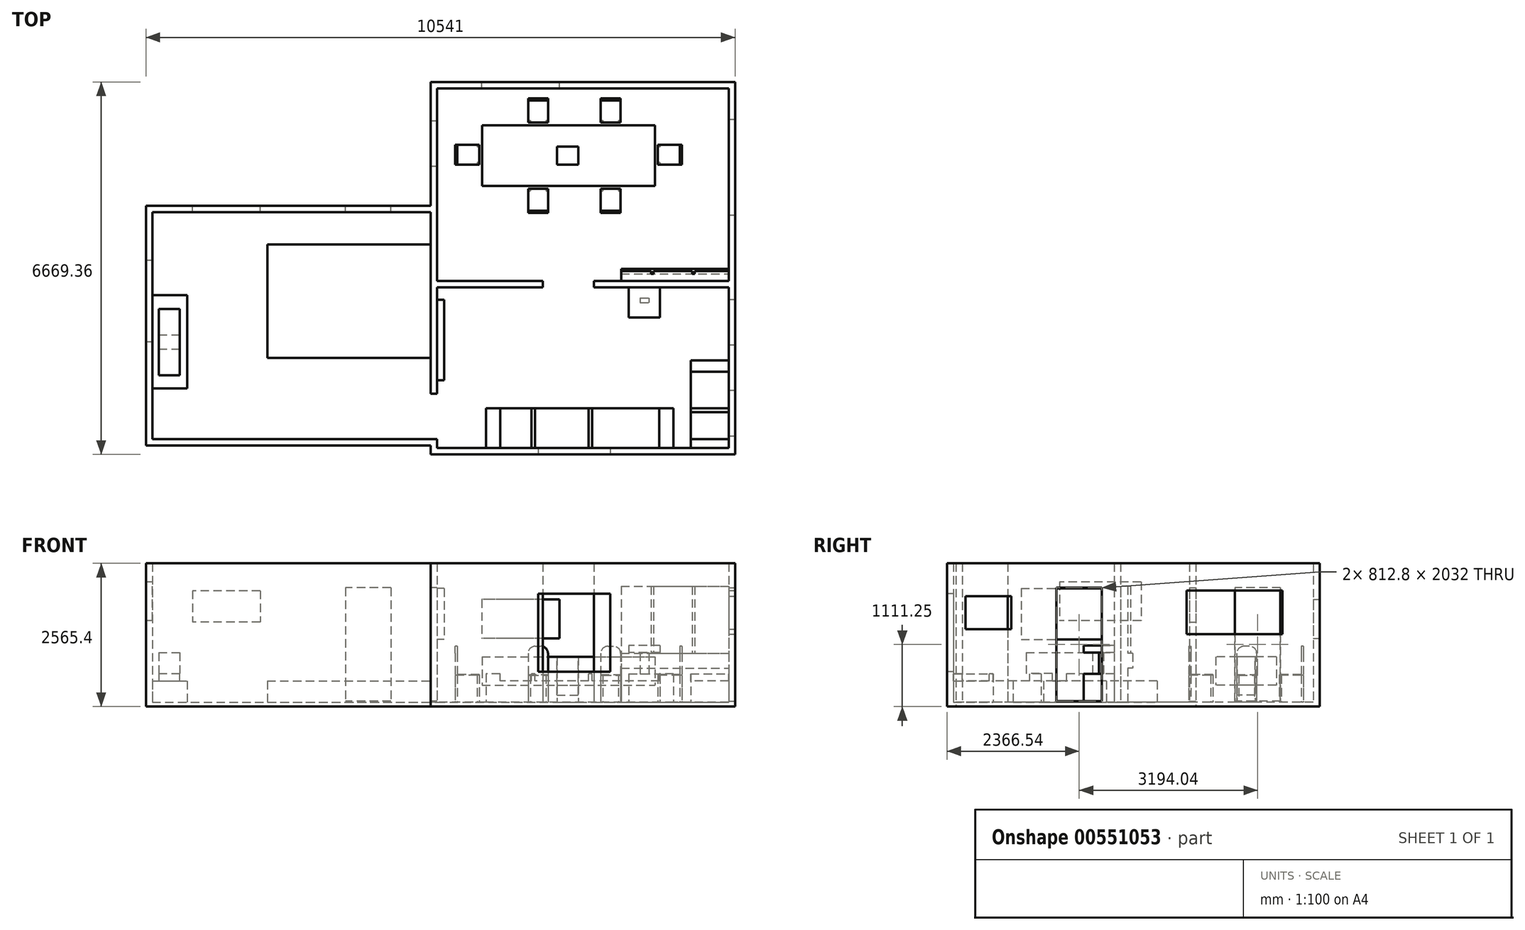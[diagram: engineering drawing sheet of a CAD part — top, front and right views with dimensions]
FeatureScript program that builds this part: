
annotation { "Feature Type Name" : "Feature", "Feature Type Description" : "" }
export const myFeature = defineFeature(function(context is Context, id is Id, definition is map)
    precondition{}
    {
        {
            var Q0;
            Q0=qCreatedBy(makeId("Top.planeOp"),FACE);
            var sketch = newSketch(context, id + "F0", { "sketchPlane" : qUnion([Q0])});
            skLineSegment(sketch, "E0", {"start": v(-1504.64, 2667.48) * mm, "end": v(-1504.64, -2915.57) * mm});
            skPoint(sketch, "E1.startSnap0", {"position": v(-1504.64, 0.48) * mm});
            skLineSegment(sketch, "E2", {"start": v(-1618.94, 335.63) * mm, "end": v(-1886.74, 335.63) * mm});
            skLineSegment(sketch, "E3", {"start": v(-6483.04, 335.63) * mm, "end": v(-6483.04, -3728.37) * mm});
            skLineSegment(sketch, "E4", {"start": v(-6483.04, -3728.37) * mm, "end": v(-1390.34, -3728.37) * mm});
            skLineSegment(sketch, "E5.0", {"start": v(-1618.94, 449.93) * mm, "end": v(-6597.34, 449.93) * mm});
            skLineSegment(sketch, "E6.0", {"start": v(-6597.34, 449.93) * mm, "end": v(-6597.34, -3842.67) * mm});
            skLineSegment(sketch, "E7.0", {"start": v(-6597.34, -3842.67) * mm, "end": v(-1504.64, -3842.67) * mm});
            skPoint(sketch, "E8.end.orphan", {"position": v(-1886.74, 335.63) * mm});
            skPoint(sketch, "E8.start.orphan", {"position": v(-2699.54, 335.63) * mm});
            skLineSegment(sketch, "E9.trimOffspring", {"start": v(-1886.74, 335.63) * mm, "end": v(-6483.04, 335.63) * mm});
            skLineSegment(sketch, "E10", {"start": v(-1618.94, 335.63) * mm, "end": v(-1504.64, 335.63) * mm});
            skLineSegment(sketch, "E11", {"start": v(-1390.34, 335.63) * mm, "end": v(-1390.34, -896.73) * mm});
            skLineSegment(sketch, "E12", {"start": v(-1390.34, 335.63) * mm, "end": v(-1390.34, 2553.18) * mm});
            skLineSegment(sketch, "E13", {"start": v(-1618.94, 449.93) * mm, "end": v(-1504.64, 449.93) * mm});
            skLineSegment(sketch, "E14", {"start": v(-1390.34, -3842.67) * mm, "end": v(-1390.34, -3728.37) * mm});
            skPoint(sketch, "E15.orphan", {"position": v(-1504.64, -3728.37) * mm});
            skLineSegment(sketch, "E16", {"start": v(-1390.34, -2915.57) * mm, "end": v(-1504.64, -2915.57) * mm});
            skLineSegment(sketch, "E17", {"start": v(-1390.34, 2667.48) * mm, "end": v(3943.66, 2667.48) * mm});
            skLineSegment(sketch, "E18", {"start": v(3943.66, 2667.48) * mm, "end": v(3943.66, -4001.88) * mm});
            skLineSegment(sketch, "E19", {"start": v(3943.66, -4001.88) * mm, "end": v(-1390.34, -4001.88) * mm});
            skLineSegment(sketch, "E20", {"start": v(-1390.34, -3887.58) * mm, "end": v(-1390.34, -3842.67) * mm});
            skLineSegment(sketch, "E21.0", {"start": v(-1390.34, -896.73) * mm, "end": v(505.29, -896.73) * mm});
            skLineSegment(sketch, "E22.0", {"start": v(-1390.34, -1011.03) * mm, "end": v(505.29, -1011.03) * mm});
            skLineSegment(sketch, "E23", {"start": v(1418.62, -1011.03) * mm, "end": v(1418.62, -896.73) * mm});
            skLineSegment(sketch, "E24.0", {"start": v(505.29, -1011.03) * mm, "end": v(505.29, -896.73) * mm});
            skLineSegment(sketch, "E25.0", {"start": v(3967.22, -3887.58) * mm, "end": v(3943.66, -3887.58) * mm});
            skLineSegment(sketch, "E26.0", {"start": v(3829.36, 2553.18) * mm, "end": v(3829.36, -896.73) * mm});
            skLineSegment(sketch, "E27.0", {"start": v(-1390.34, 2553.18) * mm, "end": v(3829.36, 2553.18) * mm});
            skLineSegment(sketch, "E28.trimOffspring", {"start": v(1418.62, -1011.03) * mm, "end": v(3829.36, -1011.03) * mm});
            skLineSegment(sketch, "E29.trimOffspring", {"start": v(1418.62, -896.73) * mm, "end": v(3829.36, -896.73) * mm});
            skLineSegment(sketch, "E30", {"start": v(-1504.64, 2667.48) * mm, "end": v(-1390.34, 2667.48) * mm});
            skLineSegment(sketch, "E31", {"start": v(-1390.34, -4001.88) * mm, "end": v(-1504.64, -4001.88) * mm});
            skLineSegment(sketch, "E32", {"start": v(-1504.64, -4001.88) * mm, "end": v(-1504.64, -3842.67) * mm});
            skLineSegment(sketch, "E33.trimOffspring", {"start": v(-1390.34, -1011.03) * mm, "end": v(-1390.34, -2915.57) * mm});
            skLineSegment(sketch, "E34.trimOffspring", {"start": v(3829.36, -3887.58) * mm, "end": v(-1390.34, -3887.58) * mm});
            skLineSegment(sketch, "E35.trimOffspring", {"start": v(3829.36, -1011.03) * mm, "end": v(3829.36, -3887.58) * mm});
            skSolve(sketch);
        }
        {
            var Q0;
            Q0=makeQuery(id+"F0.imprint","IMPRINT",FACE,{"disambiguationData":[TD([[makeQuery(id+"F0.imprint","IMPRINT",EDGE,{"derivedFrom":sQuery(id+"F0.wireOp",EDGE,"E2")}),-1.0]])]});
            extrude(context, id + "F1", {"entities" : qUnion([Q0]), "depth" : 2489.2 * mm, "offsetDistance" : 25.4 * mm});
        }
        {
            var Q0;
            {var subQ0=sQuery(id+"F0.wireOp",EDGE,"E0");Q0=makeQuery(id+"F1.opExtrude","SWEPT_FACE",FACE,{"disambiguationData":[OSD([subQ0]),TDD([makeQuery(id+"F0.imprint","IMPRINT",EDGE,{"disambiguationData":[TD([[makeQuery(id+"F0.imprint","INTERSECT",VERTEX,{"derivedFrom":[subQ0,sQuery(id+"F0.wireOp",EDGE,"E30")]}),-1.0]])],"derivedFrom":subQ0})])]});}
            var sketch = newSketch(context, id + "F2", { "sketchPlane" : qUnion([Q0])});
            skLineSegment(sketch, "E36.0.0", {"start": v(-2667.48, 0) * mm, "end": v(-449.93, 0) * mm});
            skLineSegment(sketch, "E36.0.1", {"start": v(-449.93, 0) * mm, "end": v(-449.93, 2489.2) * mm});
            skLineSegment(sketch, "E36.0.2", {"start": v(-449.93, 2489.2) * mm, "end": v(-2667.48, 2489.2) * mm});
            skLineSegment(sketch, "E36.0.3", {"start": v(-2667.48, 2489.2) * mm, "end": v(-2667.48, 0) * mm});
            skLineSegment(sketch, "E37.bottom", {"start": v(-1965.1, 19.05) * mm, "end": v(-1152.3, 19.05) * mm});
            skLineSegment(sketch, "E37.top", {"start": v(-1965.1, 2051.05) * mm, "end": v(-1152.3, 2051.05) * mm});
            skLineSegment(sketch, "E37.left", {"start": v(-1965.1, 19.05) * mm, "end": v(-1965.1, 2051.05) * mm});
            skLineSegment(sketch, "E37.right", {"start": v(-1152.3, 19.05) * mm, "end": v(-1152.3, 2051.05) * mm});
            skSolve(sketch);
        }
        {
            var Q0;
            Q0=makeQuery(id+"F2.imprint","IMPRINT",FACE,{"disambiguationData":[TD([[makeQuery(id+"F2.imprint","IMPRINT",EDGE,{"derivedFrom":sQuery(id+"F2.wireOp",EDGE,"E37.bottom")}),1.0]])]});
            extrude(context, id + "F3", {"entities" : qUnion([Q0]), "operationType" : NewBodyOperationType.REMOVE, "oppositeDirection" : true, "depth" : 1270 * mm, "offsetDistance" : 25.4 * mm});
        }
        {
            var Q0;
            Q0=makeQuery(id+"F1.opExtrude","SWEPT_FACE",FACE,{"disambiguationData":[OSD([sQuery(id+"F0.wireOp",EDGE,"E5.0"),sQuery(id+"F0.wireOp",EDGE,"E13")])]});
            var sketch = newSketch(context, id + "F4", { "sketchPlane" : qUnion([Q0])});
            skLineSegment(sketch, "E38.0", {"start": v(1504.64, 2489.2) * mm, "end": v(1504.64, 0) * mm});
            skLineSegment(sketch, "E39.0", {"start": v(6597.34, 2489.2) * mm, "end": v(1504.64, 2489.2) * mm});
            skLineSegment(sketch, "E40.0", {"start": v(6597.34, 0) * mm, "end": v(1504.64, 0) * mm});
            skLineSegment(sketch, "E41.bottom", {"start": v(2213.37, 2051.05) * mm, "end": v(3026.17, 2051.05) * mm});
            skLineSegment(sketch, "E41.top", {"start": v(2213.37, 19.05) * mm, "end": v(3026.17, 19.05) * mm});
            skLineSegment(sketch, "E41.left", {"start": v(2213.37, 2051.05) * mm, "end": v(2213.37, 19.05) * mm});
            skLineSegment(sketch, "E41.right", {"start": v(3026.17, 2051.05) * mm, "end": v(3026.17, 19.05) * mm});
            skLineSegment(sketch, "E42.bottom", {"start": v(4550.44, 1995.7) * mm, "end": v(5763.92, 1995.7) * mm});
            skLineSegment(sketch, "E42.top", {"start": v(4550.44, 1433.9) * mm, "end": v(5763.92, 1433.9) * mm});
            skLineSegment(sketch, "E42.left", {"start": v(4550.44, 1995.7) * mm, "end": v(4550.44, 1433.9) * mm});
            skLineSegment(sketch, "E42.right", {"start": v(5763.92, 1995.7) * mm, "end": v(5763.92, 1433.9) * mm});
            skSolve(sketch);
        }
        {
            var Q0;
            Q0=makeQuery(id+"F4.imprint","IMPRINT",FACE,{"disambiguationData":[TD([[makeQuery(id+"F4.imprint","IMPRINT",EDGE,{"derivedFrom":sQuery(id+"F4.wireOp",EDGE,"E41.bottom")}),-1.0]])]});
            var Q1;
            Q1=makeQuery(id+"F4.imprint","IMPRINT",FACE,{"disambiguationData":[TD([[makeQuery(id+"F4.imprint","IMPRINT",EDGE,{"derivedFrom":sQuery(id+"F4.wireOp",EDGE,"E42.bottom")}),-1.0]])]});
            extrude(context, id + "F5", {"entities" : qUnion([Q0, Q1]), "operationType" : NewBodyOperationType.REMOVE, "oppositeDirection" : true, "depth" : 508 * mm, "offsetDistance" : 25.4 * mm});
        }
        {
            var Q0;
            Q0=makeQuery(id+"F1.opExtrude","SWEPT_FACE",FACE,{"disambiguationData":[OSD([sQuery(id+"F0.wireOp",EDGE,"E17"),sQuery(id+"F0.wireOp",EDGE,"E30")])]});
            var sketch = newSketch(context, id + "F6", { "sketchPlane" : qUnion([Q0])});
            skLineSegment(sketch, "E43.0", {"start": v(1504.64, 2489.2) * mm, "end": v(-3943.66, 2489.2) * mm});
            skLineSegment(sketch, "E44.bottom", {"start": v(-805.35, 1839.46) * mm, "end": v(587.9, 1839.46) * mm});
            skLineSegment(sketch, "E44.top", {"start": v(-805.35, 1142.83) * mm, "end": v(587.9, 1142.83) * mm});
            skLineSegment(sketch, "E44.left", {"start": v(-805.35, 1839.46) * mm, "end": v(-805.35, 1142.83) * mm});
            skLineSegment(sketch, "E44.right", {"start": v(587.9, 1839.46) * mm, "end": v(587.9, 1142.83) * mm});
            skSolve(sketch);
        }
        {
            var Q0;
            Q0=makeQuery(id+"F6.imprint","IMPRINT",FACE,{"disambiguationData":[TD([[makeQuery(id+"F6.imprint","IMPRINT",EDGE,{"derivedFrom":sQuery(id+"F6.wireOp",EDGE,"E44.bottom")}),-1.0]])]});
            extrude(context, id + "F7", {"entities" : qUnion([Q0]), "operationType" : NewBodyOperationType.REMOVE, "oppositeDirection" : true, "depth" : 508 * mm, "offsetDistance" : 25.4 * mm});
        }
        {
            var Q0;
            Q0=makeQuery(id+"F1.opExtrude","SWEPT_FACE",FACE,{"disambiguationData":[OSD([sQuery(id+"F0.wireOp",EDGE,"E18")])]});
            var sketch = newSketch(context, id + "F8", { "sketchPlane" : qUnion([Q0])});
            skPoint(sketch, "E45.0", {"position": v(2553.18, 1244.6) * mm});
            skLineSegment(sketch, "E46.0", {"start": v(-896.73, 2489.2) * mm, "end": v(-896.73, 0) * mm});
            skLineSegment(sketch, "E47.0", {"start": v(2553.18, 2489.2) * mm, "end": v(2553.18, 0) * mm});
            skLineSegment(sketch, "E48.bottom", {"start": v(-2041.74, 2051.05) * mm, "end": v(-1228.94, 2051.05) * mm});
            skLineSegment(sketch, "E48.top", {"start": v(-2041.74, 19.05) * mm, "end": v(-1228.94, 19.05) * mm});
            skLineSegment(sketch, "E48.left", {"start": v(-2041.74, 2051.05) * mm, "end": v(-2041.74, 19.05) * mm});
            skLineSegment(sketch, "E48.right", {"start": v(-1228.94, 2051.05) * mm, "end": v(-1228.94, 19.05) * mm});
            skLineSegment(sketch, "E49.bottom", {"start": v(-248.45, 1994.32) * mm, "end": v(1166.3, 1994.32) * mm});
            skLineSegment(sketch, "E49.top", {"start": v(-248.45, 1469.1) * mm, "end": v(1166.3, 1469.1) * mm});
            skLineSegment(sketch, "E49.left", {"start": v(-248.45, 1994.32) * mm, "end": v(-248.45, 1469.1) * mm});
            skLineSegment(sketch, "E49.right", {"start": v(1166.3, 1994.32) * mm, "end": v(1166.3, 1469.1) * mm});
            skLineSegment(sketch, "E50.bottom", {"start": v(-3669.42, 1899.68) * mm, "end": v(-2850.85, 1899.68) * mm});
            skLineSegment(sketch, "E50.top", {"start": v(-3669.42, 1308.23) * mm, "end": v(-2850.85, 1308.23) * mm});
            skLineSegment(sketch, "E50.left", {"start": v(-3669.42, 1899.68) * mm, "end": v(-3669.42, 1308.23) * mm});
            skLineSegment(sketch, "E50.right", {"start": v(-2850.85, 1899.68) * mm, "end": v(-2850.85, 1308.23) * mm});
            skSolve(sketch);
        }
        {
            var Q0;
            Q0=makeQuery(id+"F1.opExtrude","SWEPT_FACE",FACE,{"disambiguationData":[OSD([sQuery(id+"F0.wireOp",EDGE,"E6.0")])]});
            var sketch = newSketch(context, id + "F9", { "sketchPlane" : qUnion([Q0])});
            skLineSegment(sketch, "E51.bottom", {"start": v(527.62, 2155.2) * mm, "end": v(1989.7, 2155.2) * mm});
            skLineSegment(sketch, "E51.top", {"start": v(527.62, 1464.37) * mm, "end": v(1989.7, 1464.37) * mm});
            skLineSegment(sketch, "E51.left", {"start": v(527.62, 2155.2) * mm, "end": v(527.62, 1464.37) * mm});
            skLineSegment(sketch, "E51.right", {"start": v(1989.7, 2155.2) * mm, "end": v(1989.7, 1464.37) * mm});
            skSolve(sketch);
        }
        {
            var Q0;
            Q0=makeQuery(id+"F9.imprint","IMPRINT",FACE,{"disambiguationData":[TD([[makeQuery(id+"F9.imprint","IMPRINT",EDGE,{"derivedFrom":sQuery(id+"F9.wireOp",EDGE,"E51.bottom")}),-1.0]])]});
            extrude(context, id + "F10", {"entities" : qUnion([Q0]), "operationType" : NewBodyOperationType.REMOVE, "oppositeDirection" : true, "depth" : 381 * mm, "offsetDistance" : 25.4 * mm});
        }
        {
            var Q0;
            Q0=makeQuery(id+"F1.opExtrude","CAP_FACE",FACE,{"disambiguationData":[OSD([sQuery(id+"F0.wireOp",EDGE,"E0"),sQuery(id+"F0.wireOp",EDGE,"E2"),sQuery(id+"F0.wireOp",EDGE,"E3"),sQuery(id+"F0.wireOp",EDGE,"E4"),sQuery(id+"F0.wireOp",EDGE,"E5.0"),sQuery(id+"F0.wireOp",EDGE,"E6.0"),sQuery(id+"F0.wireOp",EDGE,"E7.0"),sQuery(id+"F0.wireOp",EDGE,"E9.trimOffspring"),sQuery(id+"F0.wireOp",EDGE,"E10"),sQuery(id+"F0.wireOp",EDGE,"E11"),sQuery(id+"F0.wireOp",EDGE,"E12"),sQuery(id+"F0.wireOp",EDGE,"E13"),sQuery(id+"F0.wireOp",EDGE,"E14"),sQuery(id+"F0.wireOp",EDGE,"E16"),sQuery(id+"F0.wireOp",EDGE,"E17"),sQuery(id+"F0.wireOp",EDGE,"E18"),sQuery(id+"F0.wireOp",EDGE,"E19"),sQuery(id+"F0.wireOp",EDGE,"E20"),sQuery(id+"F0.wireOp",EDGE,"E21.0"),sQuery(id+"F0.wireOp",EDGE,"E22.0"),sQuery(id+"F0.wireOp",EDGE,"E23"),sQuery(id+"F0.wireOp",EDGE,"E24.0"),sQuery(id+"F0.wireOp",EDGE,"E26.0"),sQuery(id+"F0.wireOp",EDGE,"E27.0"),sQuery(id+"F0.wireOp",EDGE,"E28.trimOffspring"),sQuery(id+"F0.wireOp",EDGE,"E29.trimOffspring"),sQuery(id+"F0.wireOp",EDGE,"E30"),sQuery(id+"F0.wireOp",EDGE,"E31"),sQuery(id+"F0.wireOp",EDGE,"E32"),sQuery(id+"F0.wireOp",EDGE,"E33.trimOffspring"),sQuery(id+"F0.wireOp",EDGE,"E34.trimOffspring"),sQuery(id+"F0.wireOp",EDGE,"E35.trimOffspring")])],"isStart":true});
            var sketch = newSketch(context, id + "F11", { "sketchPlane" : qUnion([Q0])});
            skLineSegment(sketch, "E52.0", {"start": v(-6597.34, 3842.67) * mm, "end": v(-1504.64, 3842.67) * mm});
            skLineSegment(sketch, "E53.0", {"start": v(3943.66, 4001.88) * mm, "end": v(-1504.64, 4001.88) * mm});
            skLineSegment(sketch, "E54.0", {"start": v(-1504.64, 4001.88) * mm, "end": v(-1504.64, 3842.67) * mm});
            skLineSegment(sketch, "E55.0", {"start": v(-1504.64, -2667.48) * mm, "end": v(3943.66, -2667.48) * mm});
            skLineSegment(sketch, "E56.0", {"start": v(-1504.64, -2667.48) * mm, "end": v(-1504.64, -449.93) * mm});
            skLineSegment(sketch, "E57.0", {"start": v(-6597.34, -449.93) * mm, "end": v(-1504.64, -449.93) * mm});
            skLineSegment(sketch, "E58.0", {"start": v(-6597.34, -449.93) * mm, "end": v(-6597.34, 3842.67) * mm});
            skLineSegment(sketch, "E59.0", {"start": v(3943.66, -2667.48) * mm, "end": v(3943.66, 4001.88) * mm});
            skSolve(sketch);
        }
        {
            var Q0;
            Q0=makeQuery(id+"F8.imprint","IMPRINT",FACE,{"disambiguationData":[TD([[makeQuery(id+"F8.imprint","IMPRINT",EDGE,{"derivedFrom":sQuery(id+"F8.wireOp",EDGE,"E48.bottom")}),-1.0]])]});
            var Q1;
            Q1=makeQuery(id+"F8.imprint","IMPRINT",FACE,{"disambiguationData":[TD([[makeQuery(id+"F8.imprint","IMPRINT",EDGE,{"derivedFrom":sQuery(id+"F8.wireOp",EDGE,"E50.bottom")}),-1.0]])]});
            extrude(context, id + "F12", {"entities" : qUnion([Q0, Q1]), "operationType" : NewBodyOperationType.REMOVE, "oppositeDirection" : true, "depth" : 381 * mm, "offsetDistance" : 25.4 * mm});
        }
        {
            var Q0;
            Q0 = qSketchRegion(id + "F11", true);
            extrude(context, id + "F13", {"entities" : qUnion([Q0]), "operationType" : NewBodyOperationType.ADD, "depth" : 76.2 * mm, "offsetDistance" : 25.4 * mm});
        }
        {
            var Q0;
            Q0=makeQuery(id+"F13.opExtrude","CAP_FACE",FACE,{"disambiguationData":[OSD([sQuery(id+"F11.wireOp",EDGE,"E52.0"),sQuery(id+"F11.wireOp",EDGE,"E53.0"),sQuery(id+"F11.wireOp",EDGE,"E54.0"),sQuery(id+"F11.wireOp",EDGE,"E55.0"),sQuery(id+"F11.wireOp",EDGE,"E56.0"),sQuery(id+"F11.wireOp",EDGE,"E57.0"),sQuery(id+"F11.wireOp",EDGE,"E58.0"),sQuery(id+"F11.wireOp",EDGE,"E59.0")])],"isStart":true});
            var sketch = newSketch(context, id + "F14", { "sketchPlane" : qUnion([Q0])});
            skLineSegment(sketch, "E60.0", {"start": v(-6483.04, 335.63) * mm, "end": v(-1504.64, 335.63) * mm});
            skLineSegment(sketch, "E61.0.2", {"start": v(-1504.64, 335.63) * mm, "end": v(-6483.04, 335.63) * mm});
            skLineSegment(sketch, "E62.bottom", {"start": v(-6483.04, -2818.82) * mm, "end": v(-5860.4, -2818.82) * mm});
            skLineSegment(sketch, "E62.top", {"start": v(-6483.04, -1151.08) * mm, "end": v(-5860.4, -1151.08) * mm});
            skLineSegment(sketch, "E62.left", {"start": v(-6483.04, -2818.82) * mm, "end": v(-6483.04, -1151.08) * mm});
            skLineSegment(sketch, "E62.right", {"start": v(-5860.4, -2818.82) * mm, "end": v(-5860.4, -1151.08) * mm});
            skLineSegment(sketch, "E63.bottom", {"start": v(-4425.64, -2272.14) * mm, "end": v(-1504.64, -2272.14) * mm});
            skLineSegment(sketch, "E63.top", {"start": v(-4425.64, -240.14) * mm, "end": v(-1504.64, -240.14) * mm});
            skLineSegment(sketch, "E63.left", {"start": v(-4425.64, -2272.14) * mm, "end": v(-4425.64, -240.14) * mm});
            skLineSegment(sketch, "E63.right", {"start": v(-1504.64, -2272.14) * mm, "end": v(-1504.64, -240.14) * mm});
            skSolve(sketch);
        }
        {
            var Q0;
            Q0 = qSketchRegion(id + "F14", true);
            extrude(context, id + "F15", {"entities" : qUnion([Q0]), "operationType" : NewBodyOperationType.ADD, "depth" : 381 * mm, "offsetDistance" : 25.4 * mm});
        }
        {
            var Q0;
            Q0=makeQuery(id+"F15.opExtrude","CAP_FACE",FACE,{"disambiguationData":[OSD([sQuery(id+"F14.wireOp",EDGE,"E62.bottom"),sQuery(id+"F14.wireOp",EDGE,"E62.top"),sQuery(id+"F14.wireOp",EDGE,"E62.left"),sQuery(id+"F14.wireOp",EDGE,"E62.right")])],"isStart":false});
            var sketch = newSketch(context, id + "F16", { "sketchPlane" : qUnion([Q0])});
            skLineSegment(sketch, "E64.bottom", {"start": v(-6367.3, -2585.93) * mm, "end": v(-5994.87, -2585.93) * mm});
            skLineSegment(sketch, "E64.top", {"start": v(-6367.3, -1394.85) * mm, "end": v(-5994.87, -1394.85) * mm});
            skLineSegment(sketch, "E64.left", {"start": v(-6367.3, -2585.93) * mm, "end": v(-6367.3, -1394.85) * mm});
            skLineSegment(sketch, "E64.right", {"start": v(-5994.87, -2585.93) * mm, "end": v(-5994.87, -1394.85) * mm});
            skSolve(sketch);
        }
        {
            var Q0;
            Q0=makeQuery(id+"F16.imprint","IMPRINT",FACE,{"disambiguationData":[TD([[makeQuery(id+"F16.imprint","IMPRINT",EDGE,{"derivedFrom":sQuery(id+"F16.wireOp",EDGE,"E64.bottom")}),1.0]])]});
            extrude(context, id + "F17", {"entities" : qUnion([Q0]), "operationType" : NewBodyOperationType.ADD, "depth" : 508 * mm, "offsetDistance" : 25.4 * mm});
        }
        {
            var Q0;
            Q0=makeQuery(id+"F17.opExtrude","SWEPT_FACE",FACE,{"disambiguationData":[OSD([sQuery(id+"F16.wireOp",EDGE,"E64.right")])]});
            var sketch = newSketch(context, id + "F18", { "sketchPlane" : qUnion([Q0])});
            skLineSegment(sketch, "E65", {"start": v(-2117.39, 381) * mm, "end": v(-2117.39, 513.68) * mm});
            skLineSegment(sketch, "E66", {"start": v(-2117.39, 513.68) * mm, "end": v(-2585.93, 513.68) * mm});
            skLineSegment(sketch, "E67", {"start": v(-2585.93, 513.68) * mm, "end": v(-2585.93, 381) * mm});
            skLineSegment(sketch, "E68", {"start": v(-2585.93, 381) * mm, "end": v(-2117.39, 381) * mm});
            skLineSegment(sketch, "E69", {"start": v(-1863.39, 381) * mm, "end": v(-1863.39, 513.68) * mm});
            skLineSegment(sketch, "E70", {"start": v(-1863.39, 513.68) * mm, "end": v(-1394.85, 513.68) * mm});
            skLineSegment(sketch, "E71", {"start": v(-1394.85, 513.68) * mm, "end": v(-1394.85, 381) * mm});
            skLineSegment(sketch, "E72", {"start": v(-1394.85, 381) * mm, "end": v(-1863.39, 381) * mm});
            skSolve(sketch);
        }
        {
            var Q0;
            Q0=makeQuery(id+"F18.imprint","IMPRINT",FACE,{"disambiguationData":[TD([[makeQuery(id+"F18.imprint","IMPRINT",EDGE,{"derivedFrom":sQuery(id+"F18.wireOp",EDGE,"E65")}),1.0]])]});
            var Q1;
            Q1=makeQuery(id+"F18.imprint","IMPRINT",FACE,{"disambiguationData":[TD([[makeQuery(id+"F18.imprint","IMPRINT",EDGE,{"derivedFrom":sQuery(id+"F18.wireOp",EDGE,"E69")}),-1.0]])]});
            extrude(context, id + "F19", {"entities" : qUnion([Q0, Q1]), "operationType" : NewBodyOperationType.REMOVE, "oppositeDirection" : true, "depth" : 398.78 * mm, "offsetDistance" : 25.4 * mm});
        }
        {
            var Q0;
            Q0=makeQuery(id+"F13.boolean.opBoolean","MERGE",FACE,{"derivedFrom":[makeQuery(id+"F1.opExtrude","SWEPT_FACE",FACE,{"disambiguationData":[OSD([sQuery(id+"F0.wireOp",EDGE,"E18")])]}),makeQuery(id+"F13.opExtrude","SWEPT_FACE",FACE,{"disambiguationData":[OSD([sQuery(id+"F11.wireOp",EDGE,"E59.0")])]})]});
            var sketch = newSketch(context, id + "F20", { "sketchPlane" : qUnion([Q0])});
            skLineSegment(sketch, "E73.bottom", {"start": v(285.24, 1999.45) * mm, "end": v(1998.27, 1999.45) * mm});
            skLineSegment(sketch, "E73.top", {"start": v(285.24, 1223.23) * mm, "end": v(1998.27, 1223.23) * mm});
            skLineSegment(sketch, "E73.left", {"start": v(285.24, 1999.45) * mm, "end": v(285.24, 1223.23) * mm});
            skLineSegment(sketch, "E73.right", {"start": v(1998.27, 1999.45) * mm, "end": v(1998.27, 1223.23) * mm});
            skSolve(sketch);
        }
        {
            var Q0;
            Q0=makeQuery(id+"F20.imprint","IMPRINT",FACE,{"disambiguationData":[TD([[makeQuery(id+"F20.imprint","IMPRINT",EDGE,{"derivedFrom":sQuery(id+"F20.wireOp",EDGE,"E73.bottom")}),-1.0]])]});
            extrude(context, id + "F21", {"entities" : qUnion([Q0]), "operationType" : NewBodyOperationType.REMOVE, "oppositeDirection" : true, "depth" : 508 * mm, "offsetDistance" : 25.4 * mm});
        }
        {
            var Q0;
            Q0=makeQuery(id+"F13.boolean.opBoolean","MERGE",FACE,{"derivedFrom":[makeQuery(id+"F1.opExtrude","SWEPT_FACE",FACE,{"disambiguationData":[OSD([sQuery(id+"F0.wireOp",EDGE,"E19"),sQuery(id+"F0.wireOp",EDGE,"E31")])]}),makeQuery(id+"F13.opExtrude","SWEPT_FACE",FACE,{"disambiguationData":[OSD([sQuery(id+"F11.wireOp",EDGE,"E53.0")])]})]});
            var sketch = newSketch(context, id + "F22", { "sketchPlane" : qUnion([Q0])});
            skLineSegment(sketch, "E74.bottom", {"start": v(418.78, 1942.4) * mm, "end": v(1713.72, 1942.4) * mm});
            skLineSegment(sketch, "E74.top", {"start": v(418.78, 545.4) * mm, "end": v(1713.72, 545.4) * mm});
            skLineSegment(sketch, "E74.left", {"start": v(418.78, 1942.4) * mm, "end": v(418.78, 545.4) * mm});
            skLineSegment(sketch, "E74.right", {"start": v(1713.72, 1942.4) * mm, "end": v(1713.72, 545.4) * mm});
            skSolve(sketch);
        }
        {
            var Q0;
            Q0=makeQuery(id+"F22.imprint","IMPRINT",FACE,{"disambiguationData":[TD([[makeQuery(id+"F22.imprint","IMPRINT",EDGE,{"derivedFrom":sQuery(id+"F22.wireOp",EDGE,"E74.bottom")}),-1.0]])]});
            extrude(context, id + "F23", {"entities" : qUnion([Q0]), "operationType" : NewBodyOperationType.REMOVE, "oppositeDirection" : true, "depth" : 254 * mm, "offsetDistance" : 25.4 * mm});
        }
        {
            var Q0;
            Q0=makeQuery(id+"F1.opExtrude","SWEPT_FACE",FACE,{"disambiguationData":[OSD([sQuery(id+"F0.wireOp",EDGE,"E33.trimOffspring")])]});
            var sketch = newSketch(context, id + "F24", { "sketchPlane" : qUnion([Q0])});
            skLineSegment(sketch, "E75.bottom", {"start": v(-2675, 2039.3) * mm, "end": v(-1233.72, 2039.3) * mm});
            skLineSegment(sketch, "E75.top", {"start": v(-2675, 1123.92) * mm, "end": v(-1233.72, 1123.92) * mm});
            skLineSegment(sketch, "E75.left", {"start": v(-2675, 2039.3) * mm, "end": v(-2675, 1123.92) * mm});
            skLineSegment(sketch, "E75.right", {"start": v(-1233.72, 2039.3) * mm, "end": v(-1233.72, 1123.92) * mm});
            skSolve(sketch);
        }
        {
            var Q0;
            Q0=makeQuery(id+"F24.imprint","IMPRINT",FACE,{"disambiguationData":[TD([[makeQuery(id+"F24.imprint","IMPRINT",EDGE,{"derivedFrom":sQuery(id+"F24.wireOp",EDGE,"E75.bottom")}),-1.0]])]});
            extrude(context, id + "F25", {"entities" : qUnion([Q0]), "operationType" : NewBodyOperationType.ADD, "depth" : 127 * mm, "offsetDistance" : 25.4 * mm});
        }
        {
            var Q0;
            Q0=makeQuery(id+"F13.opExtrude","CAP_FACE",FACE,{"disambiguationData":[OSD([sQuery(id+"F11.wireOp",EDGE,"E52.0"),sQuery(id+"F11.wireOp",EDGE,"E53.0"),sQuery(id+"F11.wireOp",EDGE,"E54.0"),sQuery(id+"F11.wireOp",EDGE,"E55.0"),sQuery(id+"F11.wireOp",EDGE,"E56.0"),sQuery(id+"F11.wireOp",EDGE,"E57.0"),sQuery(id+"F11.wireOp",EDGE,"E58.0"),sQuery(id+"F11.wireOp",EDGE,"E59.0")])],"isStart":true});
            var sketch = newSketch(context, id + "F26", { "sketchPlane" : qUnion([Q0])});
            skLineSegment(sketch, "E76.bottom", {"start": v(2842.39, -3887.58) * mm, "end": v(-513.06, -3887.58) * mm});
            skLineSegment(sketch, "E76.top", {"start": v(2842.39, -3173.13) * mm, "end": v(-513.06, -3173.13) * mm});
            skLineSegment(sketch, "E76.left", {"start": v(2842.39, -3887.58) * mm, "end": v(2842.39, -3173.13) * mm});
            skLineSegment(sketch, "E76.right", {"start": v(-513.06, -3887.58) * mm, "end": v(-513.06, -3173.13) * mm});
            skSolve(sketch);
        }
        {
            var Q0;
            Q0=makeQuery(id+"F26.imprint","IMPRINT",FACE,{"disambiguationData":[TD([[makeQuery(id+"F26.imprint","IMPRINT",EDGE,{"derivedFrom":sQuery(id+"F26.wireOp",EDGE,"E76.bottom")}),-1.0]])]});
            extrude(context, id + "F27", {"entities" : qUnion([Q0]), "operationType" : NewBodyOperationType.ADD, "depth" : 508 * mm, "offsetDistance" : 25.4 * mm});
        }
        {
            var Q0;
            Q0=makeQuery(id+"F27.opExtrude","CAP_FACE",FACE,{"disambiguationData":[OSD([sQuery(id+"F26.wireOp",EDGE,"E76.bottom"),sQuery(id+"F26.wireOp",EDGE,"E76.top"),sQuery(id+"F26.wireOp",EDGE,"E76.left"),sQuery(id+"F26.wireOp",EDGE,"E76.right")])],"isStart":false});
            var sketch = newSketch(context, id + "F28", { "sketchPlane" : qUnion([Q0])});
            skLineSegment(sketch, "E77.bottom", {"start": v(2588.39, -3887.58) * mm, "end": v(1387.88, -3887.58) * mm});
            skLineSegment(sketch, "E77.top", {"start": v(2588.39, -3173.13) * mm, "end": v(1387.88, -3173.13) * mm});
            skLineSegment(sketch, "E77.left", {"start": v(2588.39, -3887.58) * mm, "end": v(2588.39, -3173.13) * mm});
            skLineSegment(sketch, "E77.right", {"start": v(1387.88, -3887.58) * mm, "end": v(1387.88, -3173.13) * mm});
            skLineSegment(sketch, "E78.bottom", {"start": v(1324.38, -3887.58) * mm, "end": v(362.76, -3887.58) * mm});
            skLineSegment(sketch, "E78.top", {"start": v(1324.38, -3173.13) * mm, "end": v(362.76, -3173.13) * mm});
            skLineSegment(sketch, "E78.left", {"start": v(1324.38, -3887.58) * mm, "end": v(1324.38, -3173.13) * mm});
            skLineSegment(sketch, "E78.right", {"start": v(362.76, -3887.58) * mm, "end": v(362.76, -3173.13) * mm});
            skLineSegment(sketch, "E79.bottom", {"start": v(299.26, -3887.58) * mm, "end": v(-259.06, -3887.58) * mm});
            skLineSegment(sketch, "E79.top", {"start": v(299.26, -3173.13) * mm, "end": v(-259.06, -3173.13) * mm});
            skLineSegment(sketch, "E79.left", {"start": v(299.26, -3887.58) * mm, "end": v(299.26, -3173.13) * mm});
            skLineSegment(sketch, "E79.right", {"start": v(-259.06, -3887.58) * mm, "end": v(-259.06, -3173.13) * mm});
            skSolve(sketch);
        }
        {
            var Q0;
            Q0 = qSketchRegion(id + "F28", true);
            extrude(context, id + "F29", {"entities" : qUnion([Q0]), "operationType" : NewBodyOperationType.REMOVE, "oppositeDirection" : true, "depth" : 127 * mm, "offsetDistance" : 25.4 * mm});
        }
        {
            var Q0;
            Q0=makeQuery(id+"F13.opExtrude","CAP_FACE",FACE,{"disambiguationData":[OSD([sQuery(id+"F11.wireOp",EDGE,"E52.0"),sQuery(id+"F11.wireOp",EDGE,"E53.0"),sQuery(id+"F11.wireOp",EDGE,"E54.0"),sQuery(id+"F11.wireOp",EDGE,"E55.0"),sQuery(id+"F11.wireOp",EDGE,"E56.0"),sQuery(id+"F11.wireOp",EDGE,"E57.0"),sQuery(id+"F11.wireOp",EDGE,"E58.0"),sQuery(id+"F11.wireOp",EDGE,"E59.0")])],"isStart":true});
            var sketch = newSketch(context, id + "F30", { "sketchPlane" : qUnion([Q0])});
            skLineSegment(sketch, "E80.bottom", {"start": v(3829.36, -2317.58) * mm, "end": v(3150.51, -2317.58) * mm});
            skLineSegment(sketch, "E80.top", {"start": v(3829.36, -3887.58) * mm, "end": v(3150.51, -3887.58) * mm});
            skLineSegment(sketch, "E80.left", {"start": v(3829.36, -2317.58) * mm, "end": v(3829.36, -3887.58) * mm});
            skLineSegment(sketch, "E80.right", {"start": v(3150.51, -2317.58) * mm, "end": v(3150.51, -3887.58) * mm});
            skSolve(sketch);
        }
        {
            var Q0;
            Q0 = qSketchRegion(id + "F30", true);
            extrude(context, id + "F31", {"entities" : qUnion([Q0]), "operationType" : NewBodyOperationType.ADD, "depth" : 508 * mm, "offsetDistance" : 25.4 * mm});
        }
        {
            var Q0;
            Q0=makeQuery(id+"F31.opExtrude","CAP_FACE",FACE,{"disambiguationData":[OSD([sQuery(id+"F30.wireOp",EDGE,"E80.bottom"),sQuery(id+"F30.wireOp",EDGE,"E80.top"),sQuery(id+"F30.wireOp",EDGE,"E80.left"),sQuery(id+"F30.wireOp",EDGE,"E80.right")])],"isStart":false});
            var sketch = newSketch(context, id + "F32", { "sketchPlane" : qUnion([Q0])});
            skLineSegment(sketch, "E81.bottom", {"start": v(3150.51, -2521.52) * mm, "end": v(3829.36, -2521.52) * mm});
            skLineSegment(sketch, "E81.top", {"start": v(3150.51, -3175.93) * mm, "end": v(3829.36, -3175.93) * mm});
            skLineSegment(sketch, "E81.left", {"start": v(3150.51, -2521.52) * mm, "end": v(3150.51, -3175.93) * mm});
            skLineSegment(sketch, "E81.right", {"start": v(3829.36, -2521.52) * mm, "end": v(3829.36, -3175.93) * mm});
            skLineSegment(sketch, "E82.bottom", {"start": v(3829.36, -3245.4) * mm, "end": v(3150.51, -3245.4) * mm});
            skLineSegment(sketch, "E82.top", {"start": v(3829.36, -3729.8) * mm, "end": v(3150.51, -3729.8) * mm});
            skLineSegment(sketch, "E82.left", {"start": v(3829.36, -3245.4) * mm, "end": v(3829.36, -3729.8) * mm});
            skLineSegment(sketch, "E82.right", {"start": v(3150.51, -3245.4) * mm, "end": v(3150.51, -3729.8) * mm});
            skSolve(sketch);
        }
        {
            var Q0;
            Q0 = qSketchRegion(id + "F32", true);
            extrude(context, id + "F33", {"entities" : qUnion([Q0]), "operationType" : NewBodyOperationType.REMOVE, "oppositeDirection" : true, "depth" : 127 * mm, "offsetDistance" : 25.4 * mm});
        }
        {
            var Q0;
            Q0=makeQuery(id+"F13.opExtrude","CAP_FACE",FACE,{"disambiguationData":[OSD([sQuery(id+"F11.wireOp",EDGE,"E52.0"),sQuery(id+"F11.wireOp",EDGE,"E53.0"),sQuery(id+"F11.wireOp",EDGE,"E54.0"),sQuery(id+"F11.wireOp",EDGE,"E55.0"),sQuery(id+"F11.wireOp",EDGE,"E56.0"),sQuery(id+"F11.wireOp",EDGE,"E57.0"),sQuery(id+"F11.wireOp",EDGE,"E58.0"),sQuery(id+"F11.wireOp",EDGE,"E59.0")])],"isStart":true});
            var sketch = newSketch(context, id + "F34", { "sketchPlane" : qUnion([Q0])});
            skLineSegment(sketch, "E83.bottom", {"start": v(2040.86, -1011.03) * mm, "end": v(2599.87, -1011.03) * mm});
            skLineSegment(sketch, "E83.top", {"start": v(2040.86, -1553.24) * mm, "end": v(2599.87, -1553.24) * mm});
            skLineSegment(sketch, "E83.left", {"start": v(2040.86, -1011.03) * mm, "end": v(2040.86, -1553.24) * mm});
            skLineSegment(sketch, "E83.right", {"start": v(2599.87, -1011.03) * mm, "end": v(2599.87, -1553.24) * mm});
            skSolve(sketch);
        }
        {
            var Q0;
            Q0 = qSketchRegion(id + "F34", true);
            extrude(context, id + "F35", {"entities" : qUnion([Q0]), "operationType" : NewBodyOperationType.ADD, "depth" : 508 * mm, "offsetDistance" : 25.4 * mm});
        }
        {
            var Q0;
            Q0=makeQuery(id+"F35.opExtrude","CAP_FACE",FACE,{"disambiguationData":[OSD([sQuery(id+"F34.wireOp",EDGE,"E83.bottom"),sQuery(id+"F34.wireOp",EDGE,"E83.top"),sQuery(id+"F34.wireOp",EDGE,"E83.left"),sQuery(id+"F34.wireOp",EDGE,"E83.right")])],"isStart":false});
            var sketch = newSketch(context, id + "F36", { "sketchPlane" : qUnion([Q0])});
            skPoint(sketch, "E84.oppositeSnap0", {"position": v(2040.86, -1282.14) * mm});
            skLineSegment(sketch, "E84.bottom", {"start": v(2243.9, -1202.24) * mm, "end": v(2404.3, -1202.24) * mm});
            skLineSegment(sketch, "E84.top", {"start": v(2243.9, -1282.14) * mm, "end": v(2404.3, -1282.14) * mm});
            skLineSegment(sketch, "E84.left", {"start": v(2243.9, -1202.24) * mm, "end": v(2243.9, -1282.14) * mm});
            skLineSegment(sketch, "E84.right", {"start": v(2404.3, -1202.24) * mm, "end": v(2404.3, -1282.14) * mm});
            skSolve(sketch);
        }
        {
            var Q0;
            Q0 = qSketchRegion(id + "F36", true);
            extrude(context, id + "F37", {"entities" : qUnion([Q0]), "operationType" : NewBodyOperationType.ADD, "depth" : 381 * mm, "offsetDistance" : 25.4 * mm});
        }
        {
            var Q0;
            Q0=makeQuery(id+"F37.opExtrude","CAP_FACE",FACE,{"disambiguationData":[OSD([sQuery(id+"F36.wireOp",EDGE,"E84.bottom"),sQuery(id+"F36.wireOp",EDGE,"E84.top"),sQuery(id+"F36.wireOp",EDGE,"E84.left"),sQuery(id+"F36.wireOp",EDGE,"E84.right")])],"isStart":false});
            var sketch = newSketch(context, id + "F38", { "sketchPlane" : qUnion([Q0])});
            skLineSegment(sketch, "E85.0.0", {"start": v(2599.87, -1553.24) * mm, "end": v(2599.87, -1011.03) * mm});
            skLineSegment(sketch, "E85.0.1", {"start": v(2599.87, -1011.03) * mm, "end": v(2040.86, -1011.03) * mm});
            skLineSegment(sketch, "E85.0.2", {"start": v(2040.86, -1011.03) * mm, "end": v(2040.86, -1553.24) * mm});
            skLineSegment(sketch, "E85.0.3", {"start": v(2040.86, -1553.24) * mm, "end": v(2599.87, -1553.24) * mm});
            skLineSegment(sketch, "E86.bottom", {"start": v(2040.86, -1011.03) * mm, "end": v(2599.87, -1011.03) * mm});
            skLineSegment(sketch, "E86.right", {"start": v(2599.87, -1011.03) * mm, "end": v(2599.87, -1553.24) * mm});
            skSolve(sketch);
        }
        {
            var Q0;
            Q0 = qSketchRegion(id + "F38", true);
            extrude(context, id + "F39", {"entities" : qUnion([Q0]), "operationType" : NewBodyOperationType.ADD, "depth" : 127 * mm, "offsetDistance" : 25.4 * mm});
        }
        {
            var Q0;
            Q0=makeQuery(id+"F13.opExtrude","CAP_FACE",FACE,{"disambiguationData":[OSD([sQuery(id+"F11.wireOp",EDGE,"E52.0"),sQuery(id+"F11.wireOp",EDGE,"E53.0"),sQuery(id+"F11.wireOp",EDGE,"E54.0"),sQuery(id+"F11.wireOp",EDGE,"E55.0"),sQuery(id+"F11.wireOp",EDGE,"E56.0"),sQuery(id+"F11.wireOp",EDGE,"E57.0"),sQuery(id+"F11.wireOp",EDGE,"E58.0"),sQuery(id+"F11.wireOp",EDGE,"E59.0")])],"isStart":true});
            var sketch = newSketch(context, id + "F40", { "sketchPlane" : qUnion([Q0])});
            skLineSegment(sketch, "E87.bottom", {"start": v(755.04, 1511.24) * mm, "end": v(1140.64, 1511.24) * mm});
            skLineSegment(sketch, "E87.top", {"start": v(755.04, 1187.97) * mm, "end": v(1140.64, 1187.97) * mm});
            skLineSegment(sketch, "E87.left", {"start": v(755.04, 1511.24) * mm, "end": v(755.04, 1187.97) * mm});
            skLineSegment(sketch, "E87.right", {"start": v(1140.64, 1511.24) * mm, "end": v(1140.64, 1187.97) * mm});
            skSolve(sketch);
        }
        {
            var Q0;
            Q0 = qSketchRegion(id + "F40", true);
            extrude(context, id + "F41", {"entities" : qUnion([Q0]), "operationType" : NewBodyOperationType.ADD, "depth" : 304.8 * mm, "offsetDistance" : 25.4 * mm});
        }
        {
            var Q0;
            Q0=makeQuery(id+"F41.opExtrude","CAP_FACE",FACE,{"disambiguationData":[OSD([sQuery(id+"F40.wireOp",EDGE,"E87.bottom"),sQuery(id+"F40.wireOp",EDGE,"E87.top"),sQuery(id+"F40.wireOp",EDGE,"E87.left"),sQuery(id+"F40.wireOp",EDGE,"E87.right")])],"isStart":false});
            var sketch = newSketch(context, id + "F42", { "sketchPlane" : qUnion([Q0])});
            skLineSegment(sketch, "E88.0.0", {"start": v(755.04, 1511.24) * mm, "end": v(755.04, 1187.97) * mm});
            skLineSegment(sketch, "E88.0.1", {"start": v(755.04, 1187.97) * mm, "end": v(1140.64, 1187.97) * mm});
            skLineSegment(sketch, "E88.0.2", {"start": v(1140.64, 1187.97) * mm, "end": v(1140.64, 1511.24) * mm});
            skLineSegment(sketch, "E88.0.3", {"start": v(1140.64, 1511.24) * mm, "end": v(755.04, 1511.24) * mm});
            skLineSegment(sketch, "E89.bottom", {"start": v(-583.52, 1892.24) * mm, "end": v(2513.74, 1892.24) * mm});
            skLineSegment(sketch, "E89.top", {"start": v(-583.52, 806.97) * mm, "end": v(2513.74, 806.97) * mm});
            skLineSegment(sketch, "E89.left", {"start": v(-583.52, 1892.24) * mm, "end": v(-583.52, 806.97) * mm});
            skLineSegment(sketch, "E89.right", {"start": v(2513.74, 1892.24) * mm, "end": v(2513.74, 806.97) * mm});
            skSolve(sketch);
        }
        {
            var Q0;
            Q0=makeQuery(id+"F42.imprint","IMPRINT",FACE,{"disambiguationData":[TD([[makeQuery(id+"F42.imprint","IMPRINT",EDGE,{"derivedFrom":sQuery(id+"F42.wireOp",EDGE,"E88.0.0")}),-1.0]])]});
            extrude(context, id + "F43", {"entities" : qUnion([Q0]), "depth" : 508 * mm, "offsetDistance" : 25.4 * mm});
        }
        {
            var Q0;
            Q0=makeQuery(id+"F43.opExtrude","CAP_FACE",FACE,{"disambiguationData":[OSD([sQuery(id+"F42.wireOp",EDGE,"E88.0.0"),sQuery(id+"F42.wireOp",EDGE,"E88.0.1"),sQuery(id+"F42.wireOp",EDGE,"E88.0.2"),sQuery(id+"F42.wireOp",EDGE,"E88.0.3"),sQuery(id+"F42.wireOp",EDGE,"E89.bottom"),sQuery(id+"F42.wireOp",EDGE,"E89.top"),sQuery(id+"F42.wireOp",EDGE,"E89.left"),sQuery(id+"F42.wireOp",EDGE,"E89.right")])],"isStart":false});
            var sketch = newSketch(context, id + "F44", { "sketchPlane" : qUnion([Q0])});
            skLineSegment(sketch, "E90.bottom", {"start": v(755.04, 1511.24) * mm, "end": v(1140.64, 1511.24) * mm});
            skLineSegment(sketch, "E90.top", {"start": v(755.04, 1187.97) * mm, "end": v(1140.64, 1187.97) * mm});
            skLineSegment(sketch, "E90.left", {"start": v(755.04, 1511.24) * mm, "end": v(755.04, 1187.97) * mm});
            skLineSegment(sketch, "E90.right", {"start": v(1140.64, 1511.24) * mm, "end": v(1140.64, 1187.97) * mm});
            skSolve(sketch);
        }
        {
            var Q0;
            Q0 = qSketchRegion(id + "F44", true);
            extrude(context, id + "F45", {"entities" : qUnion([Q0]), "oppositeDirection" : true, "depth" : 685.8 * mm, "offsetDistance" : 25.4 * mm});
        }
        {
            var Q0;
            Q0=makeQuery(id+"F13.opExtrude","CAP_FACE",FACE,{"disambiguationData":[OSD([sQuery(id+"F11.wireOp",EDGE,"E52.0"),sQuery(id+"F11.wireOp",EDGE,"E53.0"),sQuery(id+"F11.wireOp",EDGE,"E54.0"),sQuery(id+"F11.wireOp",EDGE,"E55.0"),sQuery(id+"F11.wireOp",EDGE,"E56.0"),sQuery(id+"F11.wireOp",EDGE,"E57.0"),sQuery(id+"F11.wireOp",EDGE,"E58.0"),sQuery(id+"F11.wireOp",EDGE,"E59.0")])],"isStart":true});
            var sketch = newSketch(context, id + "F46", { "sketchPlane" : qUnion([Q0])});
            skLineSegment(sketch, "E91.bottom", {"start": v(240.82, 756.17) * mm, "end": v(278.92, 756.17) * mm});
            skLineSegment(sketch, "E91.top", {"start": v(240.82, 718.07) * mm, "end": v(278.92, 718.07) * mm});
            skLineSegment(sketch, "E91.left", {"start": v(240.82, 756.17) * mm, "end": v(240.82, 718.07) * mm});
            skLineSegment(sketch, "E91.right", {"start": v(278.92, 756.17) * mm, "end": v(278.92, 718.07) * mm});
            skLineSegment(sketch, "E92.bottom", {"start": v(558.32, 756.17) * mm, "end": v(596.42, 756.17) * mm});
            skLineSegment(sketch, "E92.top", {"start": v(558.32, 718.07) * mm, "end": v(596.42, 718.07) * mm});
            skLineSegment(sketch, "E92.left", {"start": v(558.32, 756.17) * mm, "end": v(558.32, 718.07) * mm});
            skLineSegment(sketch, "E92.right", {"start": v(596.42, 756.17) * mm, "end": v(596.42, 718.07) * mm});
            skLineSegment(sketch, "E93.bottom", {"start": v(240.82, 362.47) * mm, "end": v(278.92, 362.47) * mm});
            skLineSegment(sketch, "E93.top", {"start": v(240.82, 324.37) * mm, "end": v(278.92, 324.37) * mm});
            skLineSegment(sketch, "E93.left", {"start": v(240.82, 362.47) * mm, "end": v(240.82, 324.37) * mm});
            skLineSegment(sketch, "E93.right", {"start": v(278.92, 362.47) * mm, "end": v(278.92, 324.37) * mm});
            skLineSegment(sketch, "E94.bottom", {"start": v(558.32, 362.47) * mm, "end": v(596.42, 362.47) * mm});
            skLineSegment(sketch, "E94.top", {"start": v(558.32, 324.37) * mm, "end": v(596.42, 324.37) * mm});
            skLineSegment(sketch, "E94.left", {"start": v(558.32, 362.47) * mm, "end": v(558.32, 324.37) * mm});
            skLineSegment(sketch, "E94.right", {"start": v(596.42, 362.47) * mm, "end": v(596.42, 324.37) * mm});
            skSolve(sketch);
        }
        {
            var Q0;
            Q0 = qSketchRegion(id + "F46", true);
            extrude(context, id + "F47", {"entities" : qUnion([Q0]), "operationType" : NewBodyOperationType.ADD, "depth" : 482.6 * mm, "offsetDistance" : 25.4 * mm});
        }
        {
            var Q0;
            Q0=makeQuery(id+"F47.opExtrude","CAP_FACE",FACE,{"disambiguationData":[OSD([sQuery(id+"F46.wireOp",EDGE,"E91.bottom"),sQuery(id+"F46.wireOp",EDGE,"E91.top"),sQuery(id+"F46.wireOp",EDGE,"E91.left"),sQuery(id+"F46.wireOp",EDGE,"E91.right")])],"isStart":false});
            var sketch = newSketch(context, id + "F48", { "sketchPlane" : qUnion([Q0])});
            skLineSegment(sketch, "E95.0.0", {"start": v(240.82, 756.17) * mm, "end": v(240.82, 718.07) * mm});
            skLineSegment(sketch, "E95.0.1", {"start": v(240.82, 718.07) * mm, "end": v(278.92, 718.07) * mm});
            skLineSegment(sketch, "E95.0.2", {"start": v(278.92, 718.07) * mm, "end": v(278.92, 756.17) * mm});
            skLineSegment(sketch, "E95.0.3", {"start": v(278.92, 756.17) * mm, "end": v(240.82, 756.17) * mm});
            skLineSegment(sketch, "E96.0.0", {"start": v(558.32, 362.47) * mm, "end": v(558.32, 324.37) * mm});
            skLineSegment(sketch, "E96.0.1", {"start": v(558.32, 324.37) * mm, "end": v(596.42, 324.37) * mm});
            skLineSegment(sketch, "E96.0.2", {"start": v(596.42, 324.37) * mm, "end": v(596.42, 362.47) * mm});
            skLineSegment(sketch, "E96.0.3", {"start": v(596.42, 362.47) * mm, "end": v(558.32, 362.47) * mm});
            skLineSegment(sketch, "E97.bottom", {"start": v(240.82, 756.17) * mm, "end": v(596.42, 756.17) * mm});
            skLineSegment(sketch, "E97.top", {"start": v(240.82, 324.37) * mm, "end": v(596.42, 324.37) * mm});
            skLineSegment(sketch, "E97.left", {"start": v(240.82, 756.17) * mm, "end": v(240.82, 324.37) * mm});
            skLineSegment(sketch, "E97.right", {"start": v(596.42, 756.17) * mm, "end": v(596.42, 324.37) * mm});
            skSolve(sketch);
        }
        {
            var Q0;
            Q0 = qSketchRegion(id + "F48", true);
            extrude(context, id + "F49", {"entities" : qUnion([Q0]), "operationType" : NewBodyOperationType.ADD, "depth" : 12.7 * mm, "offsetDistance" : 25.4 * mm});
        }
        {
            var Q0;
            Q0=makeQuery(id+"F49.opExtrude","CAP_FACE",FACE,{"disambiguationData":[OSD([sQuery(id+"F48.wireOp",EDGE,"E97.bottom"),sQuery(id+"F48.wireOp",EDGE,"E97.top"),sQuery(id+"F48.wireOp",EDGE,"E97.left"),sQuery(id+"F48.wireOp",EDGE,"E97.right")])],"isStart":false});
            var sketch = newSketch(context, id + "F50", { "sketchPlane" : qUnion([Q0])});
            skLineSegment(sketch, "E98.bottom", {"start": v(240.82, 324.37) * mm, "end": v(596.42, 324.37) * mm});
            skLineSegment(sketch, "E98.top", {"start": v(240.82, 362.47) * mm, "end": v(596.42, 362.47) * mm});
            skLineSegment(sketch, "E98.left", {"start": v(240.82, 324.37) * mm, "end": v(240.82, 362.47) * mm});
            skLineSegment(sketch, "E98.right", {"start": v(596.42, 324.37) * mm, "end": v(596.42, 362.47) * mm});
            skSolve(sketch);
        }
        {
            var Q0;
            Q0 = qSketchRegion(id + "F50", true);
            extrude(context, id + "F51", {"entities" : qUnion([Q0]), "operationType" : NewBodyOperationType.ADD, "depth" : 508 * mm, "offsetDistance" : 25.4 * mm});
        }
        {
            var Q0;
            Q0=makeQuery(id+"F51.opExtrude","CAP_EDGE",EDGE,{"disambiguationData":[OSD([sQuery(id+"F50.wireOp",EDGE,"E98.left")])],"isStart":false});
            var Q1;
            Q1=makeQuery(id+"F51.opExtrude","CAP_EDGE",EDGE,{"disambiguationData":[OSD([sQuery(id+"F50.wireOp",EDGE,"E98.right")])],"isStart":false});
            fillet(context, id + "F52", {"entities" : qUnion([Q0, Q1]), "radius" : 127 * mm, "tangentPropagation" : true, "allowEdgeOverflow" : false});
        }
        {
            var Q0;
            Q0=makeQuery(id+"F13.opExtrude","CAP_FACE",FACE,{"disambiguationData":[OSD([sQuery(id+"F11.wireOp",EDGE,"E52.0"),sQuery(id+"F11.wireOp",EDGE,"E53.0"),sQuery(id+"F11.wireOp",EDGE,"E54.0"),sQuery(id+"F11.wireOp",EDGE,"E55.0"),sQuery(id+"F11.wireOp",EDGE,"E56.0"),sQuery(id+"F11.wireOp",EDGE,"E57.0"),sQuery(id+"F11.wireOp",EDGE,"E58.0"),sQuery(id+"F11.wireOp",EDGE,"E59.0")])],"isStart":true});
            var sketch = newSketch(context, id + "F53", { "sketchPlane" : qUnion([Q0])});
            skLineSegment(sketch, "E99.bottom", {"start": v(1540.7, 756.17) * mm, "end": v(1578.8, 756.17) * mm});
            skLineSegment(sketch, "E99.top", {"start": v(1540.7, 718.07) * mm, "end": v(1578.8, 718.07) * mm});
            skLineSegment(sketch, "E99.left", {"start": v(1540.7, 756.17) * mm, "end": v(1540.7, 718.07) * mm});
            skLineSegment(sketch, "E99.right", {"start": v(1578.8, 756.17) * mm, "end": v(1578.8, 718.07) * mm});
            skLineSegment(sketch, "E100.bottom", {"start": v(1858.2, 756.17) * mm, "end": v(1896.3, 756.17) * mm});
            skLineSegment(sketch, "E100.top", {"start": v(1858.2, 718.07) * mm, "end": v(1896.3, 718.07) * mm});
            skLineSegment(sketch, "E100.left", {"start": v(1858.2, 756.17) * mm, "end": v(1858.2, 718.07) * mm});
            skLineSegment(sketch, "E100.right", {"start": v(1896.3, 756.17) * mm, "end": v(1896.3, 718.07) * mm});
            skLineSegment(sketch, "E101.bottom", {"start": v(1540.7, 362.47) * mm, "end": v(1578.8, 362.47) * mm});
            skLineSegment(sketch, "E101.top", {"start": v(1540.7, 324.37) * mm, "end": v(1578.8, 324.37) * mm});
            skLineSegment(sketch, "E101.left", {"start": v(1540.7, 362.47) * mm, "end": v(1540.7, 324.37) * mm});
            skLineSegment(sketch, "E101.right", {"start": v(1578.8, 362.47) * mm, "end": v(1578.8, 324.37) * mm});
            skLineSegment(sketch, "E102.bottom", {"start": v(1858.2, 362.47) * mm, "end": v(1896.3, 362.47) * mm});
            skLineSegment(sketch, "E102.top", {"start": v(1858.2, 324.37) * mm, "end": v(1896.3, 324.37) * mm});
            skLineSegment(sketch, "E102.left", {"start": v(1858.2, 362.47) * mm, "end": v(1858.2, 324.37) * mm});
            skLineSegment(sketch, "E102.right", {"start": v(1896.3, 362.47) * mm, "end": v(1896.3, 324.37) * mm});
            skSolve(sketch);
        }
        {
            var Q0;
            Q0=makeQuery(id+"F53.imprint","IMPRINT",FACE,{"disambiguationData":[TD([[makeQuery(id+"F53.imprint","IMPRINT",EDGE,{"derivedFrom":sQuery(id+"F53.wireOp",EDGE,"E101.bottom")}),-1.0]])]});
            var Q1;
            Q1=makeQuery(id+"F53.imprint","IMPRINT",FACE,{"disambiguationData":[TD([[makeQuery(id+"F53.imprint","IMPRINT",EDGE,{"derivedFrom":sQuery(id+"F53.wireOp",EDGE,"E102.bottom")}),-1.0]])]});
            var Q2;
            Q2=makeQuery(id+"F53.imprint","IMPRINT",FACE,{"disambiguationData":[TD([[makeQuery(id+"F53.imprint","IMPRINT",EDGE,{"derivedFrom":sQuery(id+"F53.wireOp",EDGE,"E100.bottom")}),-1.0]])]});
            var Q3;
            Q3=makeQuery(id+"F53.imprint","IMPRINT",FACE,{"disambiguationData":[TD([[makeQuery(id+"F53.imprint","IMPRINT",EDGE,{"derivedFrom":sQuery(id+"F53.wireOp",EDGE,"E99.bottom")}),-1.0]])]});
            extrude(context, id + "F54", {"entities" : qUnion([Q0, Q1, Q2, Q3]), "operationType" : NewBodyOperationType.ADD, "depth" : 482.6 * mm, "offsetDistance" : 25.4 * mm});
        }
        {
            var Q0;
            Q0=makeQuery(id+"F54.opExtrude","CAP_FACE",FACE,{"disambiguationData":[OSD([sQuery(id+"F53.wireOp",EDGE,"E99.bottom"),sQuery(id+"F53.wireOp",EDGE,"E99.top"),sQuery(id+"F53.wireOp",EDGE,"E99.left"),sQuery(id+"F53.wireOp",EDGE,"E99.right")])],"isStart":false});
            var sketch = newSketch(context, id + "F55", { "sketchPlane" : qUnion([Q0])});
            skLineSegment(sketch, "E103.0.0", {"start": v(1540.7, 756.17) * mm, "end": v(1540.7, 718.07) * mm});
            skLineSegment(sketch, "E103.0.1", {"start": v(1540.7, 718.07) * mm, "end": v(1578.8, 718.07) * mm});
            skLineSegment(sketch, "E103.0.2", {"start": v(1578.8, 718.07) * mm, "end": v(1578.8, 756.17) * mm});
            skLineSegment(sketch, "E103.0.3", {"start": v(1578.8, 756.17) * mm, "end": v(1540.7, 756.17) * mm});
            skLineSegment(sketch, "E104.0.0", {"start": v(1858.2, 362.47) * mm, "end": v(1858.2, 324.37) * mm});
            skLineSegment(sketch, "E104.0.1", {"start": v(1858.2, 324.37) * mm, "end": v(1896.3, 324.37) * mm});
            skLineSegment(sketch, "E104.0.2", {"start": v(1896.3, 324.37) * mm, "end": v(1896.3, 362.47) * mm});
            skLineSegment(sketch, "E104.0.3", {"start": v(1896.3, 362.47) * mm, "end": v(1858.2, 362.47) * mm});
            skLineSegment(sketch, "E105.bottom", {"start": v(1540.7, 756.17) * mm, "end": v(1896.3, 756.17) * mm});
            skLineSegment(sketch, "E105.top", {"start": v(1540.7, 324.37) * mm, "end": v(1896.3, 324.37) * mm});
            skLineSegment(sketch, "E105.left", {"start": v(1540.7, 756.17) * mm, "end": v(1540.7, 324.37) * mm});
            skLineSegment(sketch, "E105.right", {"start": v(1896.3, 756.17) * mm, "end": v(1896.3, 324.37) * mm});
            skSolve(sketch);
        }
        {
            var Q0;
            Q0 = qSketchRegion(id + "F55", true);
            extrude(context, id + "F56", {"entities" : qUnion([Q0]), "operationType" : NewBodyOperationType.ADD, "depth" : 12.7 * mm, "offsetDistance" : 25.4 * mm});
        }
        {
            var Q0;
            Q0=makeQuery(id+"F56.opExtrude","CAP_FACE",FACE,{"disambiguationData":[OSD([sQuery(id+"F55.wireOp",EDGE,"E105.bottom"),sQuery(id+"F55.wireOp",EDGE,"E105.top"),sQuery(id+"F55.wireOp",EDGE,"E105.left"),sQuery(id+"F55.wireOp",EDGE,"E105.right")])],"isStart":false});
            var sketch = newSketch(context, id + "F57", { "sketchPlane" : qUnion([Q0])});
            skLineSegment(sketch, "E106.bottom", {"start": v(1540.7, 324.37) * mm, "end": v(1896.3, 324.37) * mm});
            skLineSegment(sketch, "E106.top", {"start": v(1540.7, 362.47) * mm, "end": v(1896.3, 362.47) * mm});
            skLineSegment(sketch, "E106.left", {"start": v(1540.7, 324.37) * mm, "end": v(1540.7, 362.47) * mm});
            skLineSegment(sketch, "E106.right", {"start": v(1896.3, 324.37) * mm, "end": v(1896.3, 362.47) * mm});
            skSolve(sketch);
        }
        {
            var Q0;
            Q0 = qSketchRegion(id + "F57", true);
            extrude(context, id + "F58", {"entities" : qUnion([Q0]), "operationType" : NewBodyOperationType.ADD, "depth" : 508 * mm, "offsetDistance" : 25.4 * mm});
        }
        {
            var Q0;
            Q0=makeQuery(id+"F58.opExtrude","CAP_EDGE",EDGE,{"disambiguationData":[OSD([sQuery(id+"F57.wireOp",EDGE,"E106.left")])],"isStart":false});
            var Q1;
            Q1=makeQuery(id+"F58.opExtrude","CAP_EDGE",EDGE,{"disambiguationData":[OSD([sQuery(id+"F57.wireOp",EDGE,"E106.right")])],"isStart":false});
            fillet(context, id + "F59", {"entities" : qUnion([Q0, Q1]), "radius" : 127 * mm, "tangentPropagation" : true, "allowEdgeOverflow" : false});
        }
        {
            var Q0;
            Q0=makeQuery(id+"F13.opExtrude","CAP_FACE",FACE,{"disambiguationData":[OSD([sQuery(id+"F11.wireOp",EDGE,"E52.0"),sQuery(id+"F11.wireOp",EDGE,"E53.0"),sQuery(id+"F11.wireOp",EDGE,"E54.0"),sQuery(id+"F11.wireOp",EDGE,"E55.0"),sQuery(id+"F11.wireOp",EDGE,"E56.0"),sQuery(id+"F11.wireOp",EDGE,"E57.0"),sQuery(id+"F11.wireOp",EDGE,"E58.0"),sQuery(id+"F11.wireOp",EDGE,"E59.0")])],"isStart":true});
            var sketch = newSketch(context, id + "F60", { "sketchPlane" : qUnion([Q0])});
            skLineSegment(sketch, "E107.0", {"start": v(1540.7, 756.17) * mm, "end": v(1540.7, 362.47) * mm});
            skLineSegment(sketch, "E108", {"start": v(1540.7, 756.17) * mm, "end": v(1896.3, 756.17) * mm});
            skLineSegment(sketch, "E109.bottom", {"start": v(1540.7, 2374.84) * mm, "end": v(1578.8, 2374.84) * mm});
            skLineSegment(sketch, "E109.top", {"start": v(1540.7, 2336.74) * mm, "end": v(1578.8, 2336.74) * mm});
            skLineSegment(sketch, "E109.left", {"start": v(1540.7, 2374.84) * mm, "end": v(1540.7, 2336.74) * mm});
            skLineSegment(sketch, "E109.right", {"start": v(1578.8, 2374.84) * mm, "end": v(1578.8, 2336.74) * mm});
            skLineSegment(sketch, "E110.bottom", {"start": v(1858.2, 2374.84) * mm, "end": v(1896.3, 2374.84) * mm});
            skLineSegment(sketch, "E110.top", {"start": v(1858.2, 2336.74) * mm, "end": v(1896.3, 2336.74) * mm});
            skLineSegment(sketch, "E110.left", {"start": v(1858.2, 2374.84) * mm, "end": v(1858.2, 2336.74) * mm});
            skLineSegment(sketch, "E110.right", {"start": v(1896.3, 2374.84) * mm, "end": v(1896.3, 2336.74) * mm});
            skLineSegment(sketch, "E111.bottom", {"start": v(1540.7, 1981.14) * mm, "end": v(1578.8, 1981.14) * mm});
            skLineSegment(sketch, "E111.top", {"start": v(1540.7, 1943.04) * mm, "end": v(1578.8, 1943.04) * mm});
            skLineSegment(sketch, "E111.left", {"start": v(1540.7, 1981.14) * mm, "end": v(1540.7, 1943.04) * mm});
            skLineSegment(sketch, "E111.right", {"start": v(1578.8, 1981.14) * mm, "end": v(1578.8, 1943.04) * mm});
            skLineSegment(sketch, "E112.bottom", {"start": v(1858.2, 1981.14) * mm, "end": v(1896.3, 1981.14) * mm});
            skLineSegment(sketch, "E112.top", {"start": v(1858.2, 1943.04) * mm, "end": v(1896.3, 1943.04) * mm});
            skLineSegment(sketch, "E112.left", {"start": v(1858.2, 1981.14) * mm, "end": v(1858.2, 1943.04) * mm});
            skLineSegment(sketch, "E112.right", {"start": v(1896.3, 1981.14) * mm, "end": v(1896.3, 1943.04) * mm});
            skSolve(sketch);
        }
        {
            var Q0;
            Q0=makeQuery(id+"F60.imprint","IMPRINT",FACE,{"disambiguationData":[TD([[makeQuery(id+"F60.imprint","IMPRINT",EDGE,{"derivedFrom":sQuery(id+"F60.wireOp",EDGE,"E109.bottom")}),-1.0]])]});
            var Q1;
            Q1=makeQuery(id+"F60.imprint","IMPRINT",FACE,{"disambiguationData":[TD([[makeQuery(id+"F60.imprint","IMPRINT",EDGE,{"derivedFrom":sQuery(id+"F60.wireOp",EDGE,"E111.bottom")}),-1.0]])]});
            var Q2;
            Q2=makeQuery(id+"F60.imprint","IMPRINT",FACE,{"disambiguationData":[TD([[makeQuery(id+"F60.imprint","IMPRINT",EDGE,{"derivedFrom":sQuery(id+"F60.wireOp",EDGE,"E112.bottom")}),-1.0]])]});
            var Q3;
            Q3=makeQuery(id+"F60.imprint","IMPRINT",FACE,{"disambiguationData":[TD([[makeQuery(id+"F60.imprint","IMPRINT",EDGE,{"derivedFrom":sQuery(id+"F60.wireOp",EDGE,"E110.bottom")}),-1.0]])]});
            extrude(context, id + "F61", {"entities" : qUnion([Q0, Q1, Q2, Q3]), "operationType" : NewBodyOperationType.ADD, "depth" : 482.6 * mm, "offsetDistance" : 25.4 * mm});
        }
        {
            var Q0;
            Q0=makeQuery(id+"F61.opExtrude","CAP_FACE",FACE,{"disambiguationData":[OSD([sQuery(id+"F60.wireOp",EDGE,"E109.bottom"),sQuery(id+"F60.wireOp",EDGE,"E109.top"),sQuery(id+"F60.wireOp",EDGE,"E109.left"),sQuery(id+"F60.wireOp",EDGE,"E109.right")])],"isStart":false});
            var sketch = newSketch(context, id + "F62", { "sketchPlane" : qUnion([Q0])});
            skLineSegment(sketch, "E113.0.0", {"start": v(1540.7, 2374.84) * mm, "end": v(1540.7, 2336.74) * mm});
            skLineSegment(sketch, "E113.0.1", {"start": v(1540.7, 2336.74) * mm, "end": v(1578.8, 2336.74) * mm});
            skLineSegment(sketch, "E113.0.2", {"start": v(1578.8, 2336.74) * mm, "end": v(1578.8, 2374.84) * mm});
            skLineSegment(sketch, "E113.0.3", {"start": v(1578.8, 2374.84) * mm, "end": v(1540.7, 2374.84) * mm});
            skLineSegment(sketch, "E114.0.0", {"start": v(1858.2, 1981.14) * mm, "end": v(1858.2, 1943.04) * mm});
            skLineSegment(sketch, "E114.0.1", {"start": v(1858.2, 1943.04) * mm, "end": v(1896.3, 1943.04) * mm});
            skLineSegment(sketch, "E114.0.2", {"start": v(1896.3, 1943.04) * mm, "end": v(1896.3, 1981.14) * mm});
            skLineSegment(sketch, "E114.0.3", {"start": v(1896.3, 1981.14) * mm, "end": v(1858.2, 1981.14) * mm});
            skLineSegment(sketch, "E115.bottom", {"start": v(1540.7, 2374.84) * mm, "end": v(1896.3, 2374.84) * mm});
            skLineSegment(sketch, "E115.top", {"start": v(1540.7, 1943.04) * mm, "end": v(1896.3, 1943.04) * mm});
            skLineSegment(sketch, "E115.left", {"start": v(1540.7, 2374.84) * mm, "end": v(1540.7, 1943.04) * mm});
            skLineSegment(sketch, "E115.right", {"start": v(1896.3, 2374.84) * mm, "end": v(1896.3, 1943.04) * mm});
            skSolve(sketch);
        }
        {
            var Q0;
            {var subQ3=sQuery(id+"F62.wireOp",EDGE,"E113.0.1");Q0=makeQuery(id+"F62.imprint","IMPRINT",FACE,{"disambiguationData":[TD([[makeQuery(id+"F62.imprint","IMPRINT",EDGE,{"derivedFrom":subQ3}),-1.0]])]});}
            var Q1;
            {var subQ0=sQuery(id+"F62.wireOp",EDGE,"E114.0.0");Q1=makeQuery(id+"F62.imprint","IMPRINT",FACE,{"disambiguationData":[TD([[makeQuery(id+"F62.imprint","IMPRINT",EDGE,{"derivedFrom":subQ0}),1.0]])]});}
            var Q2;
            {var subQ0=sQuery(id+"F62.wireOp",EDGE,"E113.0.1");Q2=makeQuery(id+"F62.imprint","IMPRINT",FACE,{"disambiguationData":[TD([[makeQuery(id+"F62.imprint","IMPRINT",EDGE,{"derivedFrom":subQ0}),1.0]])]});}
            extrude(context, id + "F63", {"entities" : qUnion([Q0, Q1, Q2]), "operationType" : NewBodyOperationType.ADD, "depth" : 12.7 * mm, "offsetDistance" : 25.4 * mm});
        }
        {
            var Q0;
            Q0=makeQuery(id+"F63.opExtrude","CAP_FACE",FACE,{"disambiguationData":[OSD([sQuery(id+"F62.wireOp",EDGE,"E115.bottom"),sQuery(id+"F62.wireOp",EDGE,"E115.top"),sQuery(id+"F62.wireOp",EDGE,"E115.left"),sQuery(id+"F62.wireOp",EDGE,"E115.right")])],"isStart":false});
            var sketch = newSketch(context, id + "F64", { "sketchPlane" : qUnion([Q0])});
            skLineSegment(sketch, "E116.bottom", {"start": v(1540.7, 2374.84) * mm, "end": v(1896.3, 2374.84) * mm});
            skLineSegment(sketch, "E116.top", {"start": v(1540.7, 2336.74) * mm, "end": v(1896.3, 2336.74) * mm});
            skLineSegment(sketch, "E116.left", {"start": v(1540.7, 2374.84) * mm, "end": v(1540.7, 2336.74) * mm});
            skLineSegment(sketch, "E116.right", {"start": v(1896.3, 2374.84) * mm, "end": v(1896.3, 2336.74) * mm});
            skSolve(sketch);
        }
        {
            var Q0;
            Q0 = qSketchRegion(id + "F64", true);
            extrude(context, id + "F65", {"entities" : qUnion([Q0]), "operationType" : NewBodyOperationType.ADD, "depth" : 508 * mm, "offsetDistance" : 25.4 * mm});
        }
        {
            var Q0;
            Q0=makeQuery(id+"F65.opExtrude","CAP_EDGE",EDGE,{"disambiguationData":[OSD([sQuery(id+"F64.wireOp",EDGE,"E116.left")])],"isStart":false});
            var Q1;
            Q1=makeQuery(id+"F65.opExtrude","CAP_EDGE",EDGE,{"disambiguationData":[OSD([sQuery(id+"F64.wireOp",EDGE,"E116.right")])],"isStart":false});
            fillet(context, id + "F66", {"entities" : qUnion([Q0, Q1]), "radius" : 127 * mm, "tangentPropagation" : true, "allowEdgeOverflow" : false});
        }
        {
            var Q0;
            Q0=makeQuery(id+"F13.opExtrude","CAP_FACE",FACE,{"disambiguationData":[OSD([sQuery(id+"F11.wireOp",EDGE,"E52.0"),sQuery(id+"F11.wireOp",EDGE,"E53.0"),sQuery(id+"F11.wireOp",EDGE,"E54.0"),sQuery(id+"F11.wireOp",EDGE,"E55.0"),sQuery(id+"F11.wireOp",EDGE,"E56.0"),sQuery(id+"F11.wireOp",EDGE,"E57.0"),sQuery(id+"F11.wireOp",EDGE,"E58.0"),sQuery(id+"F11.wireOp",EDGE,"E59.0")])],"isStart":true});
            var sketch = newSketch(context, id + "F67", { "sketchPlane" : qUnion([Q0])});
            skLineSegment(sketch, "E117.0", {"start": v(240.82, 756.17) * mm, "end": v(240.82, 362.47) * mm});
            skLineSegment(sketch, "E118.bottom", {"start": v(240.82, 2374.84) * mm, "end": v(278.92, 2374.84) * mm});
            skLineSegment(sketch, "E118.top", {"start": v(240.82, 2336.74) * mm, "end": v(278.92, 2336.74) * mm});
            skLineSegment(sketch, "E118.left", {"start": v(240.82, 2374.84) * mm, "end": v(240.82, 2336.74) * mm});
            skLineSegment(sketch, "E118.right", {"start": v(278.92, 2374.84) * mm, "end": v(278.92, 2336.74) * mm});
            skLineSegment(sketch, "E119.bottom", {"start": v(558.32, 2374.84) * mm, "end": v(596.42, 2374.84) * mm});
            skLineSegment(sketch, "E119.top", {"start": v(558.32, 2336.74) * mm, "end": v(596.42, 2336.74) * mm});
            skLineSegment(sketch, "E119.left", {"start": v(558.32, 2374.84) * mm, "end": v(558.32, 2336.74) * mm});
            skLineSegment(sketch, "E119.right", {"start": v(596.42, 2374.84) * mm, "end": v(596.42, 2336.74) * mm});
            skLineSegment(sketch, "E120.bottom", {"start": v(240.82, 1981.14) * mm, "end": v(278.92, 1981.14) * mm});
            skLineSegment(sketch, "E120.top", {"start": v(240.82, 1943.04) * mm, "end": v(278.92, 1943.04) * mm});
            skLineSegment(sketch, "E120.left", {"start": v(240.82, 1981.14) * mm, "end": v(240.82, 1943.04) * mm});
            skLineSegment(sketch, "E120.right", {"start": v(278.92, 1981.14) * mm, "end": v(278.92, 1943.04) * mm});
            skLineSegment(sketch, "E121.bottom", {"start": v(558.32, 1981.14) * mm, "end": v(596.42, 1981.14) * mm});
            skLineSegment(sketch, "E121.top", {"start": v(558.32, 1943.04) * mm, "end": v(596.42, 1943.04) * mm});
            skLineSegment(sketch, "E121.left", {"start": v(558.32, 1981.14) * mm, "end": v(558.32, 1943.04) * mm});
            skLineSegment(sketch, "E121.right", {"start": v(596.42, 1981.14) * mm, "end": v(596.42, 1943.04) * mm});
            skSolve(sketch);
        }
        {
            var Q0;
            Q0 = qSketchRegion(id + "F67", true);
            extrude(context, id + "F68", {"entities" : qUnion([Q0]), "operationType" : NewBodyOperationType.ADD, "depth" : 482.6 * mm, "offsetDistance" : 25.4 * mm});
        }
        {
            var Q0;
            Q0=makeQuery(id+"F68.opExtrude","CAP_FACE",FACE,{"disambiguationData":[OSD([sQuery(id+"F67.wireOp",EDGE,"E118.bottom"),sQuery(id+"F67.wireOp",EDGE,"E118.top"),sQuery(id+"F67.wireOp",EDGE,"E118.left"),sQuery(id+"F67.wireOp",EDGE,"E118.right")])],"isStart":false});
            var sketch = newSketch(context, id + "F69", { "sketchPlane" : qUnion([Q0])});
            skLineSegment(sketch, "E122.0.0", {"start": v(240.82, 2374.84) * mm, "end": v(240.82, 2336.74) * mm});
            skLineSegment(sketch, "E122.0.1", {"start": v(240.82, 2336.74) * mm, "end": v(278.92, 2336.74) * mm});
            skLineSegment(sketch, "E122.0.2", {"start": v(278.92, 2336.74) * mm, "end": v(278.92, 2374.84) * mm});
            skLineSegment(sketch, "E122.0.3", {"start": v(278.92, 2374.84) * mm, "end": v(240.82, 2374.84) * mm});
            skLineSegment(sketch, "E123.0.0", {"start": v(558.32, 1981.14) * mm, "end": v(558.32, 1943.04) * mm});
            skLineSegment(sketch, "E123.0.1", {"start": v(558.32, 1943.04) * mm, "end": v(596.42, 1943.04) * mm});
            skLineSegment(sketch, "E123.0.2", {"start": v(596.42, 1943.04) * mm, "end": v(596.42, 1981.14) * mm});
            skLineSegment(sketch, "E123.0.3", {"start": v(596.42, 1981.14) * mm, "end": v(558.32, 1981.14) * mm});
            skLineSegment(sketch, "E124.bottom", {"start": v(240.82, 2374.84) * mm, "end": v(596.42, 2374.84) * mm});
            skLineSegment(sketch, "E124.top", {"start": v(240.82, 1943.04) * mm, "end": v(596.42, 1943.04) * mm});
            skLineSegment(sketch, "E124.left", {"start": v(240.82, 2374.84) * mm, "end": v(240.82, 1943.04) * mm});
            skLineSegment(sketch, "E124.right", {"start": v(596.42, 2374.84) * mm, "end": v(596.42, 1943.04) * mm});
            skSolve(sketch);
        }
        {
            var Q0;
            Q0 = qSketchRegion(id + "F69", true);
            extrude(context, id + "F70", {"entities" : qUnion([Q0]), "operationType" : NewBodyOperationType.ADD, "depth" : 12.7 * mm, "offsetDistance" : 25.4 * mm});
        }
        {
            var Q0;
            Q0=makeQuery(id+"F70.opExtrude","CAP_FACE",FACE,{"disambiguationData":[OSD([sQuery(id+"F69.wireOp",EDGE,"E124.bottom"),sQuery(id+"F69.wireOp",EDGE,"E124.top"),sQuery(id+"F69.wireOp",EDGE,"E124.left"),sQuery(id+"F69.wireOp",EDGE,"E124.right")])],"isStart":false});
            var sketch = newSketch(context, id + "F71", { "sketchPlane" : qUnion([Q0])});
            skLineSegment(sketch, "E125.bottom", {"start": v(240.82, 2374.84) * mm, "end": v(596.42, 2374.84) * mm});
            skLineSegment(sketch, "E125.top", {"start": v(240.82, 2336.74) * mm, "end": v(596.42, 2336.74) * mm});
            skLineSegment(sketch, "E125.left", {"start": v(240.82, 2374.84) * mm, "end": v(240.82, 2336.74) * mm});
            skLineSegment(sketch, "E125.right", {"start": v(596.42, 2374.84) * mm, "end": v(596.42, 2336.74) * mm});
            skSolve(sketch);
        }
        {
            var Q0;
            Q0 = qSketchRegion(id + "F71", true);
            extrude(context, id + "F72", {"entities" : qUnion([Q0]), "operationType" : NewBodyOperationType.ADD, "depth" : 508 * mm, "offsetDistance" : 25.4 * mm});
        }
        {
            var Q0;
            Q0=makeQuery(id+"F72.opExtrude","CAP_EDGE",EDGE,{"disambiguationData":[OSD([sQuery(id+"F71.wireOp",EDGE,"E125.left")])],"isStart":false});
            var Q1;
            Q1=makeQuery(id+"F72.opExtrude","CAP_EDGE",EDGE,{"disambiguationData":[OSD([sQuery(id+"F71.wireOp",EDGE,"E125.right")])],"isStart":false});
            fillet(context, id + "F73", {"entities" : qUnion([Q0, Q1]), "radius" : 127 * mm, "tangentPropagation" : true, "allowEdgeOverflow" : false});
        }
        {
            var Q0;
            Q0=makeQuery(id+"F13.opExtrude","CAP_FACE",FACE,{"disambiguationData":[OSD([sQuery(id+"F11.wireOp",EDGE,"E52.0"),sQuery(id+"F11.wireOp",EDGE,"E53.0"),sQuery(id+"F11.wireOp",EDGE,"E54.0"),sQuery(id+"F11.wireOp",EDGE,"E55.0"),sQuery(id+"F11.wireOp",EDGE,"E56.0"),sQuery(id+"F11.wireOp",EDGE,"E57.0"),sQuery(id+"F11.wireOp",EDGE,"E58.0"),sQuery(id+"F11.wireOp",EDGE,"E59.0")])],"isStart":true});
            var sketch = newSketch(context, id + "F74", { "sketchPlane" : qUnion([Q0])});
            skLineSegment(sketch, "E126.bottom", {"start": v(-634.32, 1539.56) * mm, "end": v(-634.32, 1501.46) * mm});
            skLineSegment(sketch, "E126.top", {"start": v(-672.42, 1539.56) * mm, "end": v(-672.42, 1501.46) * mm});
            skLineSegment(sketch, "E126.left", {"start": v(-634.32, 1539.56) * mm, "end": v(-672.42, 1539.56) * mm});
            skLineSegment(sketch, "E126.right", {"start": v(-634.32, 1501.46) * mm, "end": v(-672.42, 1501.46) * mm});
            skLineSegment(sketch, "E127.bottom", {"start": v(-634.32, 1222.06) * mm, "end": v(-634.32, 1183.96) * mm});
            skLineSegment(sketch, "E127.top", {"start": v(-672.42, 1222.06) * mm, "end": v(-672.42, 1183.96) * mm});
            skLineSegment(sketch, "E127.left", {"start": v(-634.32, 1222.06) * mm, "end": v(-672.42, 1222.06) * mm});
            skLineSegment(sketch, "E127.right", {"start": v(-634.32, 1183.96) * mm, "end": v(-672.42, 1183.96) * mm});
            skLineSegment(sketch, "E128.bottom", {"start": v(-1028.02, 1539.56) * mm, "end": v(-1028.02, 1501.46) * mm});
            skLineSegment(sketch, "E128.top", {"start": v(-1066.12, 1539.56) * mm, "end": v(-1066.12, 1501.46) * mm});
            skLineSegment(sketch, "E128.left", {"start": v(-1028.02, 1539.56) * mm, "end": v(-1066.12, 1539.56) * mm});
            skLineSegment(sketch, "E128.right", {"start": v(-1028.02, 1501.46) * mm, "end": v(-1066.12, 1501.46) * mm});
            skLineSegment(sketch, "E129.bottom", {"start": v(-1028.02, 1222.06) * mm, "end": v(-1028.02, 1183.96) * mm});
            skLineSegment(sketch, "E129.top", {"start": v(-1066.12, 1222.06) * mm, "end": v(-1066.12, 1183.96) * mm});
            skLineSegment(sketch, "E129.left", {"start": v(-1028.02, 1222.06) * mm, "end": v(-1066.12, 1222.06) * mm});
            skLineSegment(sketch, "E129.right", {"start": v(-1028.02, 1183.96) * mm, "end": v(-1066.12, 1183.96) * mm});
            skSolve(sketch);
        }
        {
            var Q0;
            Q0=makeQuery(id+"F74.imprint","IMPRINT",FACE,{"disambiguationData":[TD([[makeQuery(id+"F74.imprint","IMPRINT",EDGE,{"derivedFrom":sQuery(id+"F74.wireOp",EDGE,"E129.bottom")}),-1.0]])]});
            var Q1;
            Q1=makeQuery(id+"F74.imprint","IMPRINT",FACE,{"disambiguationData":[TD([[makeQuery(id+"F74.imprint","IMPRINT",EDGE,{"derivedFrom":sQuery(id+"F74.wireOp",EDGE,"E128.bottom")}),-1.0]])]});
            var Q2;
            Q2=makeQuery(id+"F74.imprint","IMPRINT",FACE,{"disambiguationData":[TD([[makeQuery(id+"F74.imprint","IMPRINT",EDGE,{"derivedFrom":sQuery(id+"F74.wireOp",EDGE,"E126.bottom")}),-1.0]])]});
            var Q3;
            Q3=makeQuery(id+"F74.imprint","IMPRINT",FACE,{"disambiguationData":[TD([[makeQuery(id+"F74.imprint","IMPRINT",EDGE,{"derivedFrom":sQuery(id+"F74.wireOp",EDGE,"E127.bottom")}),-1.0]])]});
            extrude(context, id + "F75", {"entities" : qUnion([Q0, Q1, Q2, Q3]), "operationType" : NewBodyOperationType.ADD, "depth" : 482.6 * mm, "offsetDistance" : 25.4 * mm});
        }
        {
            var Q0;
            Q0=makeQuery(id+"F75.opExtrude","CAP_FACE",FACE,{"disambiguationData":[OSD([sQuery(id+"F74.wireOp",EDGE,"E129.bottom"),sQuery(id+"F74.wireOp",EDGE,"E129.top"),sQuery(id+"F74.wireOp",EDGE,"E129.left"),sQuery(id+"F74.wireOp",EDGE,"E129.right")])],"isStart":false});
            var sketch = newSketch(context, id + "F76", { "sketchPlane" : qUnion([Q0])});
            skLineSegment(sketch, "E130.0.0", {"start": v(-1028.02, 1222.06) * mm, "end": v(-1066.12, 1222.06) * mm});
            skLineSegment(sketch, "E130.0.1", {"start": v(-1066.12, 1222.06) * mm, "end": v(-1066.12, 1183.96) * mm});
            skLineSegment(sketch, "E130.0.2", {"start": v(-1066.12, 1183.96) * mm, "end": v(-1028.02, 1183.96) * mm});
            skLineSegment(sketch, "E130.0.3", {"start": v(-1028.02, 1183.96) * mm, "end": v(-1028.02, 1222.06) * mm});
            skLineSegment(sketch, "E131.0.0", {"start": v(-634.32, 1539.56) * mm, "end": v(-672.42, 1539.56) * mm});
            skLineSegment(sketch, "E131.0.1", {"start": v(-672.42, 1539.56) * mm, "end": v(-672.42, 1501.46) * mm});
            skLineSegment(sketch, "E131.0.2", {"start": v(-672.42, 1501.46) * mm, "end": v(-634.32, 1501.46) * mm});
            skLineSegment(sketch, "E131.0.3", {"start": v(-634.32, 1501.46) * mm, "end": v(-634.32, 1539.56) * mm});
            skLineSegment(sketch, "E132.bottom", {"start": v(-1066.12, 1183.96) * mm, "end": v(-634.32, 1183.96) * mm});
            skLineSegment(sketch, "E132.top", {"start": v(-1066.12, 1539.56) * mm, "end": v(-634.32, 1539.56) * mm});
            skLineSegment(sketch, "E132.left", {"start": v(-1066.12, 1183.96) * mm, "end": v(-1066.12, 1539.56) * mm});
            skLineSegment(sketch, "E132.right", {"start": v(-634.32, 1183.96) * mm, "end": v(-634.32, 1539.56) * mm});
            skSolve(sketch);
        }
        {
            var Q0;
            Q0 = qSketchRegion(id + "F76", true);
            extrude(context, id + "F77", {"entities" : qUnion([Q0]), "operationType" : NewBodyOperationType.ADD, "depth" : 12.7 * mm, "offsetDistance" : 25.4 * mm});
        }
        {
            var Q0;
            Q0=makeQuery(id+"F77.opExtrude","CAP_FACE",FACE,{"disambiguationData":[OSD([sQuery(id+"F76.wireOp",EDGE,"E132.bottom"),sQuery(id+"F76.wireOp",EDGE,"E132.top"),sQuery(id+"F76.wireOp",EDGE,"E132.left"),sQuery(id+"F76.wireOp",EDGE,"E132.right")])],"isStart":false});
            var sketch = newSketch(context, id + "F78", { "sketchPlane" : qUnion([Q0])});
            skLineSegment(sketch, "E133.bottom", {"start": v(-1066.12, 1183.96) * mm, "end": v(-1028.02, 1183.96) * mm});
            skLineSegment(sketch, "E133.top", {"start": v(-1066.12, 1539.56) * mm, "end": v(-1028.02, 1539.56) * mm});
            skLineSegment(sketch, "E133.left", {"start": v(-1066.12, 1183.96) * mm, "end": v(-1066.12, 1539.56) * mm});
            skLineSegment(sketch, "E133.right", {"start": v(-1028.02, 1183.96) * mm, "end": v(-1028.02, 1539.56) * mm});
            skSolve(sketch);
        }
        {
            var Q0;
            Q0 = qSketchRegion(id + "F78", true);
            extrude(context, id + "F79", {"entities" : qUnion([Q0]), "operationType" : NewBodyOperationType.ADD, "depth" : 508 * mm, "offsetDistance" : 25.4 * mm});
        }
        {
            var Q0;
            Q0=makeQuery(id+"F79.opExtrude","CAP_EDGE",EDGE,{"disambiguationData":[OSD([sQuery(id+"F78.wireOp",EDGE,"E133.bottom")])],"isStart":false});
            var Q1;
            Q1=makeQuery(id+"F79.opExtrude","CAP_EDGE",EDGE,{"disambiguationData":[OSD([sQuery(id+"F78.wireOp",EDGE,"E133.top")])],"isStart":false});
            fillet(context, id + "F80", {"entities" : qUnion([Q0, Q1]), "radius" : 127 * mm, "tangentPropagation" : true, "allowEdgeOverflow" : false});
        }
        {
            var Q0;
            Q0=makeQuery(id+"F13.opExtrude","CAP_FACE",FACE,{"disambiguationData":[OSD([sQuery(id+"F11.wireOp",EDGE,"E52.0"),sQuery(id+"F11.wireOp",EDGE,"E53.0"),sQuery(id+"F11.wireOp",EDGE,"E54.0"),sQuery(id+"F11.wireOp",EDGE,"E55.0"),sQuery(id+"F11.wireOp",EDGE,"E56.0"),sQuery(id+"F11.wireOp",EDGE,"E57.0"),sQuery(id+"F11.wireOp",EDGE,"E58.0"),sQuery(id+"F11.wireOp",EDGE,"E59.0")])],"isStart":true});
            var sketch = newSketch(context, id + "F81", { "sketchPlane" : qUnion([Q0])});
            skLineSegment(sketch, "E134.bottom", {"start": v(2996.34, 1539.56) * mm, "end": v(2996.34, 1501.46) * mm});
            skLineSegment(sketch, "E134.top", {"start": v(2958.24, 1539.56) * mm, "end": v(2958.24, 1501.46) * mm});
            skLineSegment(sketch, "E134.left", {"start": v(2996.34, 1539.56) * mm, "end": v(2958.24, 1539.56) * mm});
            skLineSegment(sketch, "E134.right", {"start": v(2996.34, 1501.46) * mm, "end": v(2958.24, 1501.46) * mm});
            skLineSegment(sketch, "E135.bottom", {"start": v(2996.34, 1222.06) * mm, "end": v(2996.34, 1183.96) * mm});
            skLineSegment(sketch, "E135.top", {"start": v(2958.24, 1222.06) * mm, "end": v(2958.24, 1183.96) * mm});
            skLineSegment(sketch, "E135.left", {"start": v(2996.34, 1222.06) * mm, "end": v(2958.24, 1222.06) * mm});
            skLineSegment(sketch, "E135.right", {"start": v(2996.34, 1183.96) * mm, "end": v(2958.24, 1183.96) * mm});
            skLineSegment(sketch, "E136.bottom", {"start": v(2602.64, 1539.56) * mm, "end": v(2602.64, 1501.46) * mm});
            skLineSegment(sketch, "E136.top", {"start": v(2564.54, 1539.56) * mm, "end": v(2564.54, 1501.46) * mm});
            skLineSegment(sketch, "E136.left", {"start": v(2602.64, 1539.56) * mm, "end": v(2564.54, 1539.56) * mm});
            skLineSegment(sketch, "E136.right", {"start": v(2602.64, 1501.46) * mm, "end": v(2564.54, 1501.46) * mm});
            skLineSegment(sketch, "E137.bottom", {"start": v(2602.64, 1222.06) * mm, "end": v(2602.64, 1183.96) * mm});
            skLineSegment(sketch, "E137.top", {"start": v(2564.54, 1222.06) * mm, "end": v(2564.54, 1183.96) * mm});
            skLineSegment(sketch, "E137.left", {"start": v(2602.64, 1222.06) * mm, "end": v(2564.54, 1222.06) * mm});
            skLineSegment(sketch, "E137.right", {"start": v(2602.64, 1183.96) * mm, "end": v(2564.54, 1183.96) * mm});
            skSolve(sketch);
        }
        {
            var Q0;
            Q0=makeQuery(id+"F81.imprint","IMPRINT",FACE,{"disambiguationData":[TD([[makeQuery(id+"F81.imprint","IMPRINT",EDGE,{"derivedFrom":sQuery(id+"F81.wireOp",EDGE,"E134.bottom")}),-1.0]])]});
            var Q1;
            Q1=makeQuery(id+"F81.imprint","IMPRINT",FACE,{"disambiguationData":[TD([[makeQuery(id+"F81.imprint","IMPRINT",EDGE,{"derivedFrom":sQuery(id+"F81.wireOp",EDGE,"E135.bottom")}),-1.0]])]});
            var Q2;
            Q2=makeQuery(id+"F81.imprint","IMPRINT",FACE,{"disambiguationData":[TD([[makeQuery(id+"F81.imprint","IMPRINT",EDGE,{"derivedFrom":sQuery(id+"F81.wireOp",EDGE,"E137.bottom")}),-1.0]])]});
            var Q3;
            Q3=makeQuery(id+"F81.imprint","IMPRINT",FACE,{"disambiguationData":[TD([[makeQuery(id+"F81.imprint","IMPRINT",EDGE,{"derivedFrom":sQuery(id+"F81.wireOp",EDGE,"E136.bottom")}),-1.0]])]});
            extrude(context, id + "F82", {"entities" : qUnion([Q0, Q1, Q2, Q3]), "operationType" : NewBodyOperationType.ADD, "depth" : 482.6 * mm, "offsetDistance" : 25.4 * mm});
        }
        {
            var Q0;
            Q0=makeQuery(id+"F82.opExtrude","CAP_FACE",FACE,{"disambiguationData":[OSD([sQuery(id+"F81.wireOp",EDGE,"E134.bottom"),sQuery(id+"F81.wireOp",EDGE,"E134.top"),sQuery(id+"F81.wireOp",EDGE,"E134.left"),sQuery(id+"F81.wireOp",EDGE,"E134.right")])],"isStart":false});
            var sketch = newSketch(context, id + "F83", { "sketchPlane" : qUnion([Q0])});
            skLineSegment(sketch, "E138.0.0", {"start": v(2996.34, 1539.56) * mm, "end": v(2958.24, 1539.56) * mm});
            skLineSegment(sketch, "E138.0.1", {"start": v(2958.24, 1539.56) * mm, "end": v(2958.24, 1501.46) * mm});
            skLineSegment(sketch, "E138.0.2", {"start": v(2958.24, 1501.46) * mm, "end": v(2996.34, 1501.46) * mm});
            skLineSegment(sketch, "E138.0.3", {"start": v(2996.34, 1501.46) * mm, "end": v(2996.34, 1539.56) * mm});
            skLineSegment(sketch, "E139.0.0", {"start": v(2602.64, 1222.06) * mm, "end": v(2564.54, 1222.06) * mm});
            skLineSegment(sketch, "E139.0.1", {"start": v(2564.54, 1222.06) * mm, "end": v(2564.54, 1183.96) * mm});
            skLineSegment(sketch, "E139.0.2", {"start": v(2564.54, 1183.96) * mm, "end": v(2602.64, 1183.96) * mm});
            skLineSegment(sketch, "E139.0.3", {"start": v(2602.64, 1183.96) * mm, "end": v(2602.64, 1222.06) * mm});
            skLineSegment(sketch, "E140.bottom", {"start": v(2996.34, 1539.56) * mm, "end": v(2564.54, 1539.56) * mm});
            skLineSegment(sketch, "E140.top", {"start": v(2996.34, 1183.96) * mm, "end": v(2564.54, 1183.96) * mm});
            skLineSegment(sketch, "E140.left", {"start": v(2996.34, 1539.56) * mm, "end": v(2996.34, 1183.96) * mm});
            skLineSegment(sketch, "E140.right", {"start": v(2564.54, 1539.56) * mm, "end": v(2564.54, 1183.96) * mm});
            skSolve(sketch);
        }
        {
            var Q0;
            {var subQ3=sQuery(id+"F83.wireOp",EDGE,"E138.0.1");Q0=makeQuery(id+"F83.imprint","IMPRINT",FACE,{"disambiguationData":[TD([[makeQuery(id+"F83.imprint","IMPRINT",EDGE,{"derivedFrom":subQ3}),-1.0]])]});}
            var Q1;
            {var subQ0=sQuery(id+"F83.wireOp",EDGE,"E138.0.1");Q1=makeQuery(id+"F83.imprint","IMPRINT",FACE,{"disambiguationData":[TD([[makeQuery(id+"F83.imprint","IMPRINT",EDGE,{"derivedFrom":subQ0}),1.0]])]});}
            var Q2;
            {var subQ0=sQuery(id+"F83.wireOp",EDGE,"E139.0.0");Q2=makeQuery(id+"F83.imprint","IMPRINT",FACE,{"disambiguationData":[TD([[makeQuery(id+"F83.imprint","IMPRINT",EDGE,{"derivedFrom":subQ0}),1.0]])]});}
            extrude(context, id + "F84", {"entities" : qUnion([Q0, Q1, Q2]), "operationType" : NewBodyOperationType.ADD, "depth" : 12.7 * mm, "offsetDistance" : 25.4 * mm});
        }
        {
            var Q0;
            Q0=makeQuery(id+"F84.opExtrude","CAP_FACE",FACE,{"disambiguationData":[OSD([sQuery(id+"F83.wireOp",EDGE,"E140.bottom"),sQuery(id+"F83.wireOp",EDGE,"E140.top"),sQuery(id+"F83.wireOp",EDGE,"E140.left"),sQuery(id+"F83.wireOp",EDGE,"E140.right")])],"isStart":false});
            var sketch = newSketch(context, id + "F85", { "sketchPlane" : qUnion([Q0])});
            skLineSegment(sketch, "E141.bottom", {"start": v(2996.34, 1539.56) * mm, "end": v(2958.24, 1539.56) * mm});
            skLineSegment(sketch, "E141.top", {"start": v(2996.34, 1183.96) * mm, "end": v(2958.24, 1183.96) * mm});
            skLineSegment(sketch, "E141.left", {"start": v(2996.34, 1539.56) * mm, "end": v(2996.34, 1183.96) * mm});
            skLineSegment(sketch, "E141.right", {"start": v(2958.24, 1539.56) * mm, "end": v(2958.24, 1183.96) * mm});
            skSolve(sketch);
        }
        {
            var Q0;
            Q0=makeQuery(id+"F85.imprint","IMPRINT",FACE,{"disambiguationData":[TD([[makeQuery(id+"F85.imprint","IMPRINT",EDGE,{"derivedFrom":sQuery(id+"F85.wireOp",EDGE,"E141.bottom")}),1.0]])]});
            extrude(context, id + "F86", {"entities" : qUnion([Q0]), "operationType" : NewBodyOperationType.ADD, "depth" : 508 * mm, "offsetDistance" : 25.4 * mm});
        }
        {
            var Q0;
            Q0=makeQuery(id+"F86.opExtrude","CAP_EDGE",EDGE,{"disambiguationData":[OSD([sQuery(id+"F85.wireOp",EDGE,"E141.bottom")])],"isStart":false});
            var Q1;
            Q1=makeQuery(id+"F86.opExtrude","CAP_EDGE",EDGE,{"disambiguationData":[OSD([sQuery(id+"F85.wireOp",EDGE,"E141.top")])],"isStart":false});
            fillet(context, id + "F87", {"entities" : qUnion([Q0, Q1]), "radius" : 127 * mm, "tangentPropagation" : true, "allowEdgeOverflow" : false});
        }
        {
            var Q0;
            Q0=makeQuery(id+"F1.opExtrude","SWEPT_FACE",FACE,{"disambiguationData":[OSD([sQuery(id+"F0.wireOp",EDGE,"E29.trimOffspring")])]});
            var sketch = newSketch(context, id + "F88", { "sketchPlane" : qUnion([Q0])});
            skLineSegment(sketch, "E142.bottom", {"start": v(-1906.77, 1101.2) * mm, "end": v(-3829.36, 1101.2) * mm});
            skLineSegment(sketch, "E142.top", {"start": v(-1906.77, 0) * mm, "end": v(-3829.36, 0) * mm});
            skLineSegment(sketch, "E142.left", {"start": v(-1906.77, 1101.2) * mm, "end": v(-1906.77, 0) * mm});
            skLineSegment(sketch, "E142.right", {"start": v(-3829.36, 1101.2) * mm, "end": v(-3829.36, 0) * mm});
            skLineSegment(sketch, "E143.top", {"start": v(-1906.77, 2074.53) * mm, "end": v(-3829.36, 2074.53) * mm});
            skLineSegment(sketch, "E143.left", {"start": v(-1906.77, 1101.2) * mm, "end": v(-1906.77, 2074.53) * mm});
            skLineSegment(sketch, "E143.right", {"start": v(-3829.36, 1101.2) * mm, "end": v(-3829.36, 2074.53) * mm});
            skSolve(sketch);
        }
        {
            var Q0;
            Q0 = qSketchRegion(id + "F88", true);
            extrude(context, id + "F89", {"entities" : qUnion([Q0]), "operationType" : NewBodyOperationType.ADD, "depth" : 127 * mm, "offsetDistance" : 25.4 * mm});
        }
        {
            var Q0;
            Q0=makeQuery(id+"F89.opExtrude","CAP_FACE",FACE,{"disambiguationData":[OSD([sQuery(id+"F88.wireOp",EDGE,"E142.top"),sQuery(id+"F88.wireOp",EDGE,"E142.left"),sQuery(id+"F88.wireOp",EDGE,"E142.right"),sQuery(id+"F88.wireOp",EDGE,"E143.top"),sQuery(id+"F88.wireOp",EDGE,"E143.left"),sQuery(id+"F88.wireOp",EDGE,"E143.right")])],"isStart":false});
            var sketch = newSketch(context, id + "F90", { "sketchPlane" : qUnion([Q0])});
            skLineSegment(sketch, "E144.bottom", {"start": v(-1906.77, 875.81) * mm, "end": v(-3829.36, 875.81) * mm});
            skLineSegment(sketch, "E144.top", {"start": v(-1906.77, 0) * mm, "end": v(-3829.36, 0) * mm});
            skLineSegment(sketch, "E144.left", {"start": v(-1906.77, 875.81) * mm, "end": v(-1906.77, 0) * mm});
            skLineSegment(sketch, "E144.right", {"start": v(-3829.36, 875.81) * mm, "end": v(-3829.36, 0) * mm});
            skLineSegment(sketch, "E145", {"start": v(-1906.77, 612.64) * mm, "end": v(-3829.36, 612.64) * mm});
            skSolve(sketch);
        }
        {
            var Q0;
            {var subQ0=sQuery(id+"F90.wireOp",EDGE,"E144.bottom");Q0=makeQuery(id+"F90.imprint","IMPRINT",FACE,{"disambiguationData":[TD([[makeQuery(id+"F90.imprint","IMPRINT",EDGE,{"derivedFrom":subQ0}),1.0]])]});}
            extrude(context, id + "F91", {"entities" : qUnion([Q0]), "operationType" : NewBodyOperationType.ADD, "depth" : 88.9 * mm, "offsetDistance" : 25.4 * mm});
        }
        {
            var Q0;
            {var subQ0=sQuery(id+"F88.wireOp",EDGE,"E143.top");var subQ1=sQuery(id+"F88.wireOp",EDGE,"E143.left");var subQ2=sQuery(id+"F88.wireOp",EDGE,"E142.left");Q0=makeQuery(id+"F91.boolean.opBoolean","SPLIT",FACE,{"disambiguationData":[TD([makeQuery(id+"F89.opExtrude","SWEPT_FACE",FACE,{"disambiguationData":[OSD([subQ0])]})])],"derivedFrom":makeQuery(id+"F89.opExtrude","CAP_FACE",FACE,{"disambiguationData":[OSD([sQuery(id+"F88.wireOp",EDGE,"E142.top"),subQ2,sQuery(id+"F88.wireOp",EDGE,"E142.right"),subQ0,subQ1,sQuery(id+"F88.wireOp",EDGE,"E143.right")])],"isStart":false})});}
            var sketch = newSketch(context, id + "F92", { "sketchPlane" : qUnion([Q0])});
            skLineSegment(sketch, "E146.bottom", {"start": v(-3221.9, 2074.53) * mm, "end": v(-3829.36, 2074.53) * mm});
            skLineSegment(sketch, "E146.top", {"start": v(-3221.9, 875.81) * mm, "end": v(-3829.36, 875.81) * mm});
            skLineSegment(sketch, "E146.left", {"start": v(-3221.9, 2074.53) * mm, "end": v(-3221.9, 875.81) * mm});
            skLineSegment(sketch, "E146.right", {"start": v(-3829.36, 2074.53) * mm, "end": v(-3829.36, 875.81) * mm});
            skLineSegment(sketch, "E147.bottom", {"start": v(-3178.24, 2074.53) * mm, "end": v(-2485.44, 2074.53) * mm});
            skLineSegment(sketch, "E147.top", {"start": v(-3178.24, 875.81) * mm, "end": v(-2485.44, 875.81) * mm});
            skLineSegment(sketch, "E147.left", {"start": v(-3178.24, 2074.53) * mm, "end": v(-3178.24, 875.81) * mm});
            skLineSegment(sketch, "E147.right", {"start": v(-2485.44, 2074.53) * mm, "end": v(-2485.44, 875.81) * mm});
            skLineSegment(sketch, "E148.bottom", {"start": v(-2408.26, 2074.53) * mm, "end": v(-1906.77, 2074.53) * mm});
            skLineSegment(sketch, "E148.top", {"start": v(-2408.26, 875.81) * mm, "end": v(-1906.77, 875.81) * mm});
            skLineSegment(sketch, "E148.right", {"start": v(-1906.77, 2074.53) * mm, "end": v(-1906.77, 875.81) * mm});
            skLineSegment(sketch, "E149", {"start": v(-2408.26, 2074.53) * mm, "end": v(-2439.47, 2074.53) * mm});
            skLineSegment(sketch, "E150", {"start": v(-2439.47, 2074.53) * mm, "end": v(-2439.47, 875.81) * mm});
            skLineSegment(sketch, "E151", {"start": v(-2439.47, 875.81) * mm, "end": v(-2408.26, 875.81) * mm});
            skSolve(sketch);
        }
        {
            var Q0;
            Q0 = qSketchRegion(id + "F92", true);
            extrude(context, id + "F93", {"entities" : qUnion([Q0]), "operationType" : NewBodyOperationType.ADD, "depth" : 50.8 * mm, "offsetDistance" : 25.4 * mm});
        }
        {
            var Q0;
            Q0 = qSketchRegion(id + "F92", true);
            extrude(context, id + "F94", {"entities" : qUnion([Q0]), "operationType" : NewBodyOperationType.ADD, "depth" : 25.4 * mm, "offsetDistance" : 25.4 * mm});
        }
    });
